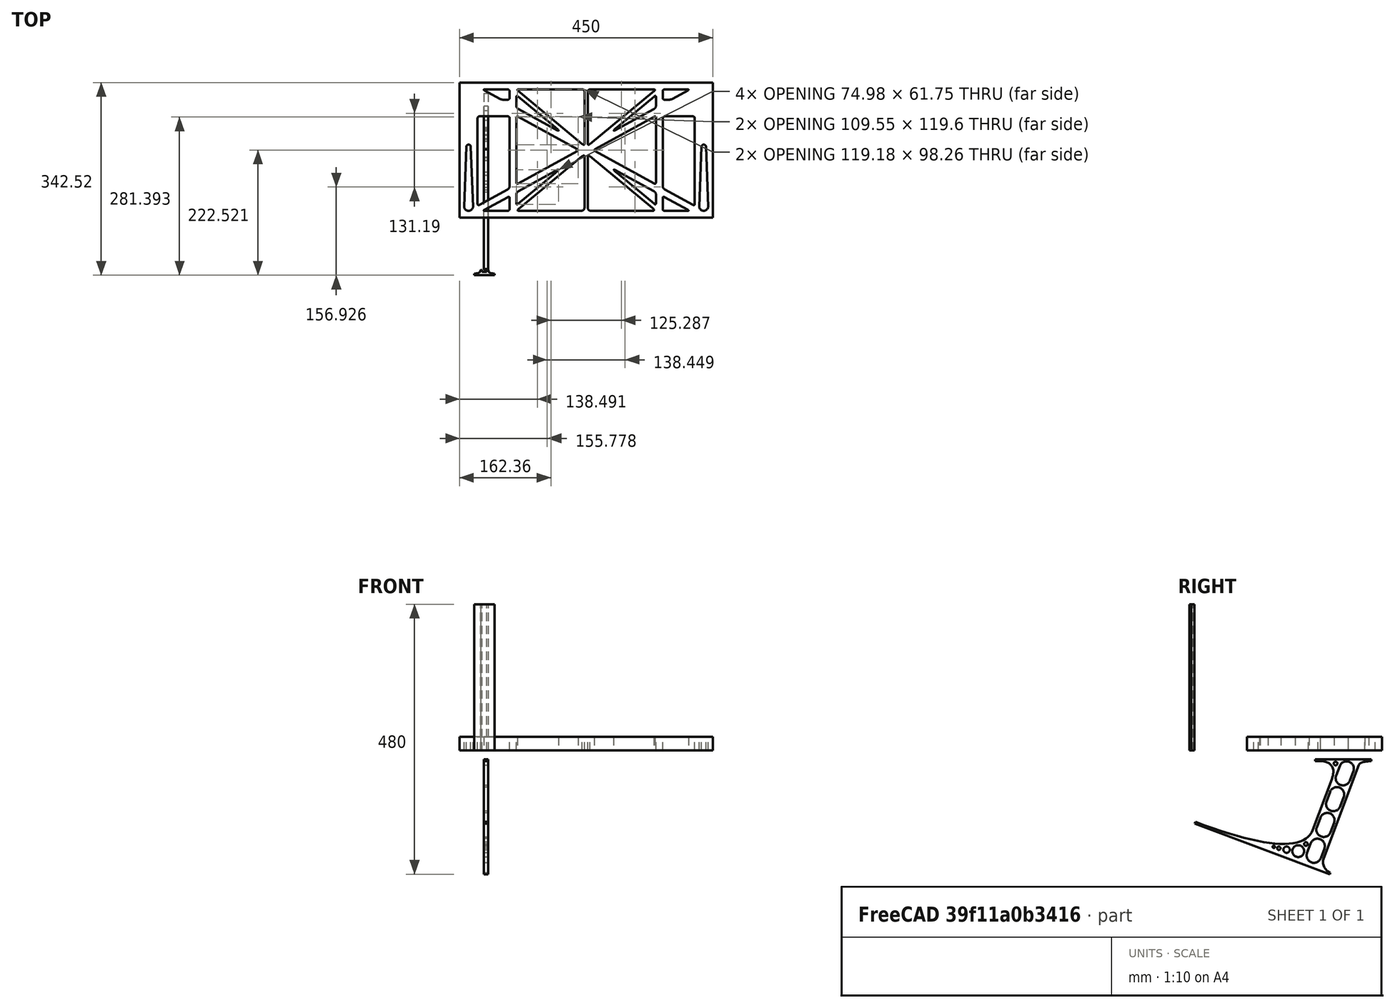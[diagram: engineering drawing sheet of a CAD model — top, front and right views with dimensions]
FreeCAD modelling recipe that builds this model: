
FCSTD DOCUMENT  (FreeCAD 0.19R0.19.2)
Label: laptopStand166FCStd
License: All rights reserved
LicenseURL: http://en.wikipedia.org/wiki/All_rights_reserved
objects: Sketcher::SketchObject×4, Part::Extrusion×3
note: 7 computed .brp shape members not serialized (recipe doc carries the construction recipe); baked Part::Feature solids carry a one-line shape summary decoded from their .brp

FEATURE [Sketcher::SketchObject] Sketch
  FullyConstrained = false
  sketch-geometry (349):
    g0: LineSegment StartX=-10.9272 StartY=-82.7794 StartZ=0 EndX=46.0728 EndY=-51.4823 EndZ=0
    g1: LineSegment StartX=-10.9272 StartY=76.4095 StartZ=0 EndX=-10.9272 EndY=-82.7794 EndZ=0
    g2: LineSegment StartX=46.0728 StartY=76.4095 StartZ=0 EndX=46.0728 EndY=-51.4823 EndZ=0
    g3: LineSegment StartX=-42.9272 StartY=136.221 StartZ=0 EndX=-42.9272 EndY=-103.779 EndZ=0
    g4: LineSegment StartX=407.073 StartY=136.221 StartZ=0 EndX=407.073 EndY=-103.779 EndZ=0
    g5: ArcOfCircle CenterX=-26.9272 CenterY=-83.7794 CenterZ=0 NormalX=0 NormalY=0 NormalZ=1 AngleXU=0 Radius=8 StartAngle=3.14159 EndAngle=6.28319
    g6: ArcOfCircle CenterX=391.073 CenterY=22.1087 CenterZ=0 NormalX=0 NormalY=0 NormalZ=1 AngleXU=0 Radius=8 StartAngle=-4.4e-15 EndAngle=3.14159
    g7: LineSegment StartX=399.073 StartY=22.1087 StartZ=0 EndX=399.073 EndY=-83.7794 EndZ=0
    g8: LineSegment StartX=383.073 StartY=22.1087 StartZ=0 EndX=383.073 EndY=-83.7794 EndZ=0
    g9: ArcOfCircle CenterX=391.073 CenterY=-83.7794 CenterZ=0 NormalX=0 NormalY=0 NormalZ=1 AngleXU=0 Radius=8 StartAngle=3.14159 EndAngle=6.28319
    g10: Circle CenterX=175.022 CenterY=27.0628 CenterZ=0 NormalX=0 NormalY=0 NormalZ=1 AngleXU=0 Radius=1
    g11: Circle CenterX=179.022 CenterY=24.8665 CenterZ=0 NormalX=0 NormalY=0 NormalZ=1 AngleXU=0 Radius=1
    g12: Circle CenterX=179.022 CenterY=27.0628 CenterZ=0 NormalX=0 NormalY=0 NormalZ=1 AngleXU=0 Radius=1
    g13: BSplineCurve PolesCount=3 KnotsCount=2 Degree=2 IsPeriodic=0
    g14: GeomPoint X=175.022 Y=27.0628 Z=0
    g15: GeomPoint X=179.022 Y=27.0628 Z=0
    g16: Circle CenterX=189.124 CenterY=27.0628 CenterZ=0 NormalX=0 NormalY=0 NormalZ=1 AngleXU=0 Radius=1
    g17: Circle CenterX=185.124 CenterY=24.8665 CenterZ=0 NormalX=0 NormalY=0 NormalZ=1 AngleXU=0 Radius=1
    g18: Circle CenterX=185.124 CenterY=27.0628 CenterZ=0 NormalX=0 NormalY=0 NormalZ=1 AngleXU=0 Radius=1
    g19: BSplineCurve PolesCount=3 KnotsCount=2 Degree=2 IsPeriodic=0
    g20: GeomPoint X=189.124 Y=27.0628 Z=0
    g21: GeomPoint X=185.124 Y=27.0628 Z=0
    g22: Circle CenterX=175.022 CenterY=5.37834 CenterZ=0 NormalX=0 NormalY=0 NormalZ=1 AngleXU=0 Radius=1
    g23: Circle CenterX=179.022 CenterY=7.57463 CenterZ=0 NormalX=0 NormalY=0 NormalZ=1 AngleXU=0 Radius=1
    g24: Circle CenterX=179.022 CenterY=5.34704 CenterZ=0 NormalX=0 NormalY=0 NormalZ=1 AngleXU=0 Radius=1
    g25: BSplineCurve PolesCount=3 KnotsCount=2 Degree=2 IsPeriodic=0
    g26: GeomPoint X=175.022 Y=5.37834 Z=0
    g27: GeomPoint X=179.022 Y=5.34704 Z=0
    g28: Circle CenterX=189.124 CenterY=5.37834 CenterZ=0 NormalX=0 NormalY=0 NormalZ=1 AngleXU=0 Radius=1
    g29: Circle CenterX=185.124 CenterY=7.57463 CenterZ=0 NormalX=0 NormalY=0 NormalZ=1 AngleXU=0 Radius=1
    g30: Circle CenterX=185.124 CenterY=5.34704 CenterZ=0 NormalX=0 NormalY=0 NormalZ=1 AngleXU=0 Radius=1
    g31: BSplineCurve PolesCount=3 KnotsCount=2 Degree=2 IsPeriodic=0
    g32: GeomPoint X=189.124 Y=5.37834 Z=0
    g33: GeomPoint X=185.124 Y=5.34704 Z=0
    g34: Circle CenterX=165.871 CenterY=18.1458 CenterZ=0 NormalX=0 NormalY=0 NormalZ=1 AngleXU=0 Radius=1
    g35: Circle CenterX=169.377 CenterY=16.2206 CenterZ=0 NormalX=0 NormalY=0 NormalZ=1 AngleXU=0 Radius=1
    g36: Circle CenterX=165.871 CenterY=14.2954 CenterZ=0 NormalX=0 NormalY=0 NormalZ=1 AngleXU=0 Radius=1
    g37: BSplineCurve PolesCount=3 KnotsCount=2 Degree=2 IsPeriodic=0
    g38: GeomPoint X=165.871 Y=18.1458 Z=0
    g39: GeomPoint X=165.871 Y=14.2954 Z=0
    g40: Circle CenterX=198.275 CenterY=18.1458 CenterZ=0 NormalX=0 NormalY=0 NormalZ=1 AngleXU=0 Radius=1
    g41: Circle CenterX=194.768 CenterY=16.2206 CenterZ=0 NormalX=0 NormalY=0 NormalZ=1 AngleXU=0 Radius=1
    g42: Circle CenterX=198.275 CenterY=14.2954 CenterZ=0 NormalX=0 NormalY=0 NormalZ=1 AngleXU=0 Radius=1
    g43: BSplineCurve PolesCount=3 KnotsCount=2 Degree=2 IsPeriodic=0
    g44: GeomPoint X=198.275 Y=18.1458 Z=0
    g45: GeomPoint X=198.275 Y=14.2954 Z=0
    g46: LineSegment StartX=407.073 StartY=-103.779 StartZ=0 EndX=-42.9272 EndY=-103.779 EndZ=0
    g47: LineSegment StartX=407.073 StartY=136.221 StartZ=0 EndX=-42.9272 EndY=136.221 EndZ=0
    g48: LineSegment StartX=46.0728 StartY=76.4095 StartZ=0 EndX=-10.9272 EndY=76.4095 EndZ=0
    g49: Circle CenterX=125.607 CenterY=54.1951 CenterZ=0 NormalX=0 NormalY=0 NormalZ=1 AngleXU=0 Radius=1
    g50: Circle CenterX=139.632 CenterY=46.4944 CenterZ=0 NormalX=0 NormalY=0 NormalZ=1 AngleXU=0 Radius=1
    g51: Circle CenterX=127.326 CenterY=56.7187 CenterZ=0 NormalX=0 NormalY=0 NormalZ=1 AngleXU=0 Radius=1
    g52: BSplineCurve PolesCount=3 KnotsCount=2 Degree=2 IsPeriodic=0
    g53: GeomPoint X=125.607 Y=54.1951 Z=0
    g54: GeomPoint X=127.326 Y=56.7187 Z=0
    g55: Circle CenterX=236.821 CenterY=56.7187 CenterZ=0 NormalX=0 NormalY=0 NormalZ=1 AngleXU=0 Radius=1
    g56: Circle CenterX=224.513 CenterY=46.4944 CenterZ=0 NormalX=0 NormalY=0 NormalZ=1 AngleXU=0 Radius=1
    g57: Circle CenterX=238.538 CenterY=54.1951 CenterZ=0 NormalX=0 NormalY=0 NormalZ=1 AngleXU=0 Radius=1
    g58: BSplineCurve PolesCount=3 KnotsCount=2 Degree=2 IsPeriodic=0
    g59: GeomPoint X=236.821 Y=56.7187 Z=0
    g60: GeomPoint X=238.538 Y=54.1951 Z=0
    g61: Circle CenterX=238.538 CenterY=-21.7539 CenterZ=0 NormalX=0 NormalY=0 NormalZ=1 AngleXU=0 Radius=1
    g62: Circle CenterX=224.513 CenterY=-14.0532 CenterZ=0 NormalX=0 NormalY=0 NormalZ=1 AngleXU=0 Radius=1
    g63: Circle CenterX=236.821 CenterY=-24.2775 CenterZ=0 NormalX=0 NormalY=0 NormalZ=1 AngleXU=0 Radius=1
    g64: BSplineCurve PolesCount=3 KnotsCount=2 Degree=2 IsPeriodic=0
    g65: GeomPoint X=238.538 Y=-21.7539 Z=0
    g66: GeomPoint X=236.821 Y=-24.2775 Z=0
    g67: Circle CenterX=125.607 CenterY=-21.7539 CenterZ=0 NormalX=0 NormalY=0 NormalZ=1 AngleXU=0 Radius=1
    g68: Circle CenterX=139.632 CenterY=-14.0532 CenterZ=0 NormalX=0 NormalY=0 NormalZ=1 AngleXU=0 Radius=1
    g69: Circle CenterX=127.325 CenterY=-24.2775 CenterZ=0 NormalX=0 NormalY=0 NormalZ=1 AngleXU=0 Radius=1
    g70: BSplineCurve PolesCount=3 KnotsCount=2 Degree=2 IsPeriodic=0
    g71: GeomPoint X=125.607 Y=-21.7539 Z=0
    g72: GeomPoint X=127.325 Y=-24.2775 Z=0
    g73: Circle CenterX=302.996 CenterY=111.695 CenterZ=0 NormalX=0 NormalY=0 NormalZ=1 AngleXU=0 Radius=1
    g74: Circle CenterX=306.073 CenterY=114.251 CenterZ=0 NormalX=0 NormalY=0 NormalZ=1 AngleXU=0 Radius=1
    g75: Circle CenterX=306.073 CenterY=110.251 CenterZ=0 NormalX=0 NormalY=0 NormalZ=1 AngleXU=0 Radius=1
    g76: BSplineCurve PolesCount=3 KnotsCount=2 Degree=2 IsPeriodic=0
    g77: GeomPoint X=302.996 Y=111.695 Z=0
    g78: GeomPoint X=306.073 Y=110.251 Z=0
    g79: Circle CenterX=306.073 CenterY=95.2763 CenterZ=0 NormalX=0 NormalY=0 NormalZ=1 AngleXU=0 Radius=1
    g80: Circle CenterX=306.073 CenterY=91.2763 CenterZ=0 NormalX=0 NormalY=0 NormalZ=1 AngleXU=0 Radius=1
    g81: Circle CenterX=302.567 CenterY=89.3511 CenterZ=0 NormalX=0 NormalY=0 NormalZ=1 AngleXU=0 Radius=1
    g82: BSplineCurve PolesCount=3 KnotsCount=2 Degree=2 IsPeriodic=0
    g83: GeomPoint X=306.073 Y=95.2763 Z=0
    g84: GeomPoint X=302.567 Y=89.3511 Z=0
    g85: LineSegment StartX=306.073 StartY=110.251 StartZ=0 EndX=306.073 EndY=95.2763 EndZ=0
    g86: LineSegment StartX=302.996 StartY=111.695 StartZ=0 EndX=236.821 EndY=56.7187 EndZ=0
    g87: LineSegment StartX=238.538 StartY=54.1951 StartZ=0 EndX=302.567 EndY=89.3511 EndZ=0
    g88: Circle CenterX=61.1496 CenterY=111.695 CenterZ=0 NormalX=0 NormalY=0 NormalZ=1 AngleXU=0 Radius=1
    g89: Circle CenterX=58.0728 CenterY=114.251 CenterZ=0 NormalX=0 NormalY=0 NormalZ=1 AngleXU=0 Radius=1
    g90: Circle CenterX=58.0728 CenterY=110.251 CenterZ=0 NormalX=0 NormalY=0 NormalZ=1 AngleXU=0 Radius=1
    g91: BSplineCurve PolesCount=3 KnotsCount=2 Degree=2 IsPeriodic=0
    g92: GeomPoint X=61.1496 Y=111.695 Z=0
    g93: GeomPoint X=58.0728 Y=110.251 Z=0
    g94: Circle CenterX=61.5791 CenterY=89.3511 CenterZ=0 NormalX=0 NormalY=0 NormalZ=1 AngleXU=0 Radius=1
    g95: Circle CenterX=58.0728 CenterY=91.2763 CenterZ=0 NormalX=0 NormalY=0 NormalZ=1 AngleXU=0 Radius=1
    g96: Circle CenterX=58.0728 CenterY=95.2763 CenterZ=0 NormalX=0 NormalY=0 NormalZ=1 AngleXU=0 Radius=1
    g97: BSplineCurve PolesCount=3 KnotsCount=2 Degree=2 IsPeriodic=0
    g98: GeomPoint X=61.5791 Y=89.3511 Z=0
    g99: GeomPoint X=58.0728 Y=95.2763 Z=0
    g100: LineSegment StartX=58.0728 StartY=110.251 StartZ=0 EndX=58.0728 EndY=95.2763 EndZ=0
    g101: LineSegment StartX=61.1496 StartY=111.695 StartZ=0 EndX=127.326 EndY=56.7187 EndZ=0
    g102: LineSegment StartX=125.607 StartY=54.1951 StartZ=0 EndX=61.5791 EndY=89.3511 EndZ=0
    g103: Circle CenterX=61.5791 CenterY=-56.9099 CenterZ=0 NormalX=0 NormalY=0 NormalZ=1 AngleXU=0 Radius=1
    g104: Circle CenterX=58.0728 CenterY=-58.8351 CenterZ=0 NormalX=0 NormalY=0 NormalZ=1 AngleXU=0 Radius=1
    g105: Circle CenterX=58.0728 CenterY=-62.8351 CenterZ=0 NormalX=0 NormalY=0 NormalZ=1 AngleXU=0 Radius=1
    g106: BSplineCurve PolesCount=3 KnotsCount=2 Degree=2 IsPeriodic=0
    g107: GeomPoint X=61.5791 Y=-56.9099 Z=0
    g108: GeomPoint X=58.0728 Y=-62.8351 Z=0
    g109: Circle CenterX=58.0728 CenterY=-77.8102 CenterZ=0 NormalX=0 NormalY=0 NormalZ=1 AngleXU=0 Radius=1
    g110: Circle CenterX=58.0728 CenterY=-81.8102 CenterZ=0 NormalX=0 NormalY=0 NormalZ=1 AngleXU=0 Radius=1
    g111: Circle CenterX=61.1496 CenterY=-79.2541 CenterZ=0 NormalX=0 NormalY=0 NormalZ=1 AngleXU=0 Radius=1
    g112: BSplineCurve PolesCount=3 KnotsCount=2 Degree=2 IsPeriodic=0
    g113: GeomPoint X=58.0728 Y=-77.8102 Z=0
    g114: GeomPoint X=61.1496 Y=-79.2541 Z=0
    g115: LineSegment StartX=58.0728 StartY=-62.8351 StartZ=0 EndX=58.0728 EndY=-77.8102 EndZ=0
    g116: LineSegment StartX=61.1496 StartY=-79.2541 StartZ=0 EndX=127.325 EndY=-24.2775 EndZ=0
    g117: LineSegment StartX=125.607 StartY=-21.7539 StartZ=0 EndX=61.5791 EndY=-56.9099 EndZ=0
    g118: Circle CenterX=302.567 CenterY=-56.9099 CenterZ=0 NormalX=0 NormalY=0 NormalZ=1 AngleXU=0 Radius=1
    g119: Circle CenterX=306.073 CenterY=-58.8351 CenterZ=0 NormalX=0 NormalY=0 NormalZ=1 AngleXU=0 Radius=1
    g120: Circle CenterX=306.073 CenterY=-62.8351 CenterZ=0 NormalX=0 NormalY=0 NormalZ=1 AngleXU=0 Radius=1
    g121: BSplineCurve PolesCount=3 KnotsCount=2 Degree=2 IsPeriodic=0
    g122: GeomPoint X=302.567 Y=-56.9099 Z=0
    g123: GeomPoint X=306.073 Y=-62.8351 Z=0
    g124: Circle CenterX=302.996 CenterY=-79.2541 CenterZ=0 NormalX=0 NormalY=0 NormalZ=1 AngleXU=0 Radius=1
    g125: Circle CenterX=306.073 CenterY=-81.8102 CenterZ=0 NormalX=0 NormalY=0 NormalZ=1 AngleXU=0 Radius=1
    g126: Circle CenterX=306.073 CenterY=-77.8102 CenterZ=0 NormalX=0 NormalY=0 NormalZ=1 AngleXU=0 Radius=1
    g127: BSplineCurve PolesCount=3 KnotsCount=2 Degree=2 IsPeriodic=0
    g128: GeomPoint X=302.996 Y=-79.2541 Z=0
    g129: GeomPoint X=306.073 Y=-77.8102 Z=0
    g130: LineSegment StartX=306.073 StartY=-62.8351 StartZ=0 EndX=306.073 EndY=-77.8102 EndZ=0
    g131: LineSegment StartX=302.996 StartY=-79.2541 StartZ=0 EndX=236.821 EndY=-24.2775 EndZ=0
    g132: LineSegment StartX=238.538 StartY=-21.7539 StartZ=0 EndX=302.567 EndY=-56.9099 EndZ=0
    g133: Circle CenterX=61.6457 CenterY=-88.8112 CenterZ=0 NormalX=0 NormalY=0 NormalZ=1 AngleXU=0 Radius=1
    g134: Circle CenterX=58.0728 CenterY=-91.7794 CenterZ=0 NormalX=0 NormalY=0 NormalZ=1 AngleXU=0 Radius=1
    g135: Circle CenterX=63.9135 CenterY=-91.7794 CenterZ=0 NormalX=0 NormalY=0 NormalZ=1 AngleXU=0 Radius=1
    g136: BSplineCurve PolesCount=3 KnotsCount=2 Degree=2 IsPeriodic=0
    g137: GeomPoint X=61.6457 Y=-88.8112 Z=0
    g138: GeomPoint X=63.9135 Y=-91.7794 Z=0
    g139: Circle CenterX=179.022 CenterY=-85.8163 CenterZ=0 NormalX=0 NormalY=0 NormalZ=1 AngleXU=0 Radius=1
    g140: Circle CenterX=179.022 CenterY=-91.7794 CenterZ=0 NormalX=0 NormalY=0 NormalZ=1 AngleXU=0 Radius=1
    g141: Circle CenterX=171.895 CenterY=-91.7794 CenterZ=0 NormalX=0 NormalY=0 NormalZ=1 AngleXU=0 Radius=1
    g142: BSplineCurve PolesCount=3 KnotsCount=2 Degree=2 IsPeriodic=0
    g143: GeomPoint X=179.022 Y=-85.8163 Z=0
    g144: GeomPoint X=171.895 Y=-91.7794 Z=0
    g145: Circle CenterX=185.124 CenterY=-86.2028 CenterZ=0 NormalX=0 NormalY=0 NormalZ=1 AngleXU=0 Radius=1
    g146: Circle CenterX=185.124 CenterY=-91.7794 CenterZ=0 NormalX=0 NormalY=0 NormalZ=1 AngleXU=0 Radius=1
    g147: Circle CenterX=191.747 CenterY=-91.7794 CenterZ=0 NormalX=0 NormalY=0 NormalZ=1 AngleXU=0 Radius=1
    g148: BSplineCurve PolesCount=3 KnotsCount=2 Degree=2 IsPeriodic=0
    g149: GeomPoint X=185.124 Y=-86.2028 Z=0
    g150: GeomPoint X=191.747 Y=-91.7794 Z=0
    g151: Circle CenterX=299.888 CenterY=-86.6413 CenterZ=0 NormalX=0 NormalY=0 NormalZ=1 AngleXU=0 Radius=1
    g152: Circle CenterX=306.073 CenterY=-91.7794 CenterZ=0 NormalX=0 NormalY=0 NormalZ=1 AngleXU=0 Radius=1
    g153: Circle CenterX=298.776 CenterY=-91.7794 CenterZ=0 NormalX=0 NormalY=0 NormalZ=1 AngleXU=0 Radius=1
    g154: BSplineCurve PolesCount=3 KnotsCount=2 Degree=2 IsPeriodic=0
    g155: GeomPoint X=299.888 Y=-86.6413 Z=0
    g156: GeomPoint X=298.776 Y=-91.7794 Z=0
    g157: LineSegment StartX=189.124 StartY=5.37834 StartZ=0 EndX=299.888 EndY=-86.6413 EndZ=0
    g158: LineSegment StartX=298.776 StartY=-91.7794 StartZ=0 EndX=191.747 EndY=-91.7794 EndZ=0
    g159: LineSegment StartX=185.124 StartY=-86.2028 StartZ=0 EndX=185.124 EndY=5.34704 EndZ=0
    g160: LineSegment StartX=179.022 StartY=5.34704 StartZ=0 EndX=179.022 EndY=-85.8163 EndZ=0
    g161: LineSegment StartX=171.895 StartY=-91.7794 StartZ=0 EndX=63.9135 EndY=-91.7794 EndZ=0
    g162: LineSegment StartX=61.6457 StartY=-88.8112 StartZ=0 EndX=175.022 EndY=5.37834 EndZ=0
    g163: Circle CenterX=302.073 CenterY=124.221 CenterZ=0 NormalX=0 NormalY=0 NormalZ=1 AngleXU=0 Radius=1
    g164: Circle CenterX=306.073 CenterY=124.221 CenterZ=0 NormalX=0 NormalY=0 NormalZ=1 AngleXU=0 Radius=1
    g165: Circle CenterX=302.996 CenterY=121.665 CenterZ=0 NormalX=0 NormalY=0 NormalZ=1 AngleXU=0 Radius=1
    g166: BSplineCurve PolesCount=3 KnotsCount=2 Degree=2 IsPeriodic=0
    g167: GeomPoint X=302.073 Y=124.221 Z=0
    g168: GeomPoint X=302.996 Y=121.665 Z=0
    g169: Circle CenterX=189.124 CenterY=124.221 CenterZ=0 NormalX=0 NormalY=0 NormalZ=1 AngleXU=0 Radius=1
    g170: Circle CenterX=185.124 CenterY=124.221 CenterZ=0 NormalX=0 NormalY=0 NormalZ=1 AngleXU=0 Radius=1
    g171: Circle CenterX=185.124 CenterY=120.221 CenterZ=0 NormalX=0 NormalY=0 NormalZ=1 AngleXU=0 Radius=1
    g172: BSplineCurve PolesCount=3 KnotsCount=2 Degree=2 IsPeriodic=0
    g173: GeomPoint X=189.124 Y=124.221 Z=0
    g174: GeomPoint X=185.124 Y=120.221 Z=0
    g175: Circle CenterX=175.022 CenterY=124.221 CenterZ=0 NormalX=0 NormalY=0 NormalZ=1 AngleXU=0 Radius=1
    g176: Circle CenterX=179.022 CenterY=124.221 CenterZ=0 NormalX=0 NormalY=0 NormalZ=1 AngleXU=0 Radius=1
    g177: Circle CenterX=179.022 CenterY=120.221 CenterZ=0 NormalX=0 NormalY=0 NormalZ=1 AngleXU=0 Radius=1
    g178: BSplineCurve PolesCount=3 KnotsCount=2 Degree=2 IsPeriodic=0
    g179: GeomPoint X=175.022 Y=124.221 Z=0
    g180: GeomPoint X=179.022 Y=120.221 Z=0
    g181: Circle CenterX=62.0728 CenterY=124.221 CenterZ=0 NormalX=0 NormalY=0 NormalZ=1 AngleXU=0 Radius=1
    g182: Circle CenterX=58.0728 CenterY=124.221 CenterZ=0 NormalX=0 NormalY=0 NormalZ=1 AngleXU=0 Radius=1
    g183: Circle CenterX=61.1496 CenterY=121.665 CenterZ=0 NormalX=0 NormalY=0 NormalZ=1 AngleXU=0 Radius=1
    g184: BSplineCurve PolesCount=3 KnotsCount=2 Degree=2 IsPeriodic=0
    g185: GeomPoint X=62.0728 Y=124.221 Z=0
    g186: GeomPoint X=61.1496 Y=121.665 Z=0
    g187: LineSegment StartX=62.0728 StartY=124.221 StartZ=0 EndX=175.022 EndY=124.221 EndZ=0
    g188: LineSegment StartX=179.022 StartY=120.221 StartZ=0 EndX=179.022 EndY=27.0628 EndZ=0
    g189: LineSegment StartX=185.124 StartY=27.0628 StartZ=0 EndX=185.124 EndY=120.221 EndZ=0
    g190: LineSegment StartX=189.124 StartY=124.221 StartZ=0 EndX=302.073 EndY=124.221 EndZ=0
    g191: LineSegment StartX=302.996 StartY=121.665 StartZ=0 EndX=189.124 EndY=27.0628 EndZ=0
    g192: LineSegment StartX=175.022 StartY=27.0628 StartZ=0 EndX=61.1496 EndY=121.665 EndZ=0
    g193: Circle CenterX=61.5791 CenterY=75.4095 CenterZ=0 NormalX=0 NormalY=0 NormalZ=1 AngleXU=0 Radius=1
    g194: Circle CenterX=58.0728 CenterY=77.3346 CenterZ=0 NormalX=0 NormalY=0 NormalZ=1 AngleXU=0 Radius=1
    g195: Circle CenterX=58.0728 CenterY=73.3346 CenterZ=0 NormalX=0 NormalY=0 NormalZ=1 AngleXU=0 Radius=1
    g196: BSplineCurve PolesCount=3 KnotsCount=2 Degree=2 IsPeriodic=0
    g197: GeomPoint X=61.5791 Y=75.4095 Z=0
    g198: GeomPoint X=58.0728 Y=73.3346 Z=0
    g199: Circle CenterX=58.0728 CenterY=-40.8935 CenterZ=0 NormalX=0 NormalY=0 NormalZ=1 AngleXU=0 Radius=1
    g200: Circle CenterX=58.0728 CenterY=-44.8935 CenterZ=0 NormalX=0 NormalY=0 NormalZ=1 AngleXU=0 Radius=1
    g201: Circle CenterX=61.5791 CenterY=-42.9683 CenterZ=0 NormalX=0 NormalY=0 NormalZ=1 AngleXU=0 Radius=1
    g202: BSplineCurve PolesCount=3 KnotsCount=2 Degree=2 IsPeriodic=0
    g203: GeomPoint X=58.0728 Y=-40.8935 Z=0
    g204: GeomPoint X=61.5791 Y=-42.9683 Z=0
    g205: LineSegment StartX=61.5791 StartY=-42.9683 StartZ=0 EndX=165.871 EndY=14.2954 EndZ=0
    g206: LineSegment StartX=165.871 StartY=18.1458 StartZ=0 EndX=61.5791 EndY=75.4095 EndZ=0
    g207: LineSegment StartX=58.0728 StartY=73.3346 StartZ=0 EndX=58.0728 EndY=-40.8935 EndZ=0
    g208: Circle CenterX=302.567 CenterY=-42.9683 CenterZ=0 NormalX=0 NormalY=0 NormalZ=1 AngleXU=0 Radius=1
    g209: Circle CenterX=306.073 CenterY=-44.8935 CenterZ=0 NormalX=0 NormalY=0 NormalZ=1 AngleXU=0 Radius=1
    g210: Circle CenterX=306.073 CenterY=-40.8935 CenterZ=0 NormalX=0 NormalY=0 NormalZ=1 AngleXU=0 Radius=1
    g211: BSplineCurve PolesCount=3 KnotsCount=2 Degree=2 IsPeriodic=0
    g212: GeomPoint X=302.567 Y=-42.9683 Z=0
    g213: GeomPoint X=306.073 Y=-40.8935 Z=0
    g214: Circle CenterX=306.073 CenterY=73.3346 CenterZ=0 NormalX=0 NormalY=0 NormalZ=1 AngleXU=0 Radius=1
    g215: Circle CenterX=306.073 CenterY=77.3346 CenterZ=0 NormalX=0 NormalY=0 NormalZ=1 AngleXU=0 Radius=1
    g216: Circle CenterX=302.567 CenterY=75.4095 CenterZ=0 NormalX=0 NormalY=0 NormalZ=1 AngleXU=0 Radius=1
    g217: BSplineCurve PolesCount=3 KnotsCount=2 Degree=2 IsPeriodic=0
    g218: GeomPoint X=306.073 Y=73.3346 Z=0
    g219: GeomPoint X=302.567 Y=75.4095 Z=0
    g220: LineSegment StartX=302.567 StartY=-42.9683 StartZ=0 EndX=198.275 EndY=14.2954 EndZ=0
    g221: LineSegment StartX=198.275 StartY=18.1458 StartZ=0 EndX=302.567 EndY=75.4095 EndZ=0
    g222: LineSegment StartX=306.073 StartY=73.3346 StartZ=0 EndX=306.073 EndY=-40.8935 EndZ=0
    g223: LineSegment StartX=322.073 StartY=105.865 StartZ=0 EndX=328.643 EndY=105.865 EndZ=0
    g224: LineSegment StartX=318.073 StartY=120.221 StartZ=0 EndX=318.073 EndY=109.865 EndZ=0
    g225: LineSegment StartX=336.157 StartY=107.779 StartZ=0 EndX=362.567 EndY=122.294 EndZ=0
    g226: Circle CenterX=362.073 CenterY=124.221 CenterZ=0 NormalX=0 NormalY=0 NormalZ=1 AngleXU=0 Radius=1
    g227: Circle CenterX=366.073 CenterY=124.221 CenterZ=0 NormalX=0 NormalY=0 NormalZ=1 AngleXU=0 Radius=1
    g228: Circle CenterX=362.567 CenterY=122.294 CenterZ=0 NormalX=0 NormalY=0 NormalZ=1 AngleXU=0 Radius=1
    g229: BSplineCurve PolesCount=3 KnotsCount=2 Degree=2 IsPeriodic=0
    g230: GeomPoint X=362.073 Y=124.221 Z=0
    g231: GeomPoint X=362.567 Y=122.294 Z=0
    g232: Circle CenterX=322.073 CenterY=124.221 CenterZ=0 NormalX=0 NormalY=0 NormalZ=1 AngleXU=0 Radius=1
    g233: Circle CenterX=318.073 CenterY=124.221 CenterZ=0 NormalX=0 NormalY=0 NormalZ=1 AngleXU=0 Radius=1
    g234: Circle CenterX=318.073 CenterY=120.221 CenterZ=0 NormalX=0 NormalY=0 NormalZ=1 AngleXU=0 Radius=1
    g235: BSplineCurve PolesCount=3 KnotsCount=2 Degree=2 IsPeriodic=0
    g236: GeomPoint X=322.073 Y=124.221 Z=0
    g237: GeomPoint X=318.073 Y=120.221 Z=0
    g238: Circle CenterX=322.073 CenterY=105.865 CenterZ=0 NormalX=0 NormalY=0 NormalZ=1 AngleXU=0 Radius=1
    g239: Circle CenterX=318.073 CenterY=105.865 CenterZ=0 NormalX=0 NormalY=0 NormalZ=1 AngleXU=0 Radius=1
    g240: Circle CenterX=318.073 CenterY=109.865 CenterZ=0 NormalX=0 NormalY=0 NormalZ=1 AngleXU=0 Radius=1
    g241: BSplineCurve PolesCount=3 KnotsCount=2 Degree=2 IsPeriodic=0
    g242: GeomPoint X=322.073 Y=105.865 Z=0
    g243: GeomPoint X=318.073 Y=109.865 Z=0
    g244: Circle CenterX=336.157 CenterY=107.779 CenterZ=0 NormalX=0 NormalY=0 NormalZ=1 AngleXU=0 Radius=1
    g245: Circle CenterX=332.651 CenterY=105.853 CenterZ=0 NormalX=0 NormalY=0 NormalZ=1 AngleXU=0 Radius=1
    g246: Circle CenterX=328.643 CenterY=105.865 CenterZ=0 NormalX=0 NormalY=0 NormalZ=1 AngleXU=0 Radius=1
    g247: BSplineCurve PolesCount=3 KnotsCount=2 Degree=2 IsPeriodic=0
    g248: GeomPoint X=336.157 Y=107.779 Z=0
    g249: GeomPoint X=328.643 Y=105.865 Z=0
    g250: LineSegment StartX=322.073 StartY=124.221 StartZ=0 EndX=362.073 EndY=124.221 EndZ=0
    g251: Circle CenterX=371.567 CenterY=-80.8644 CenterZ=0 NormalX=0 NormalY=0 NormalZ=1 AngleXU=0 Radius=1
    g252: Circle CenterX=375.073 CenterY=-82.7896 CenterZ=0 NormalX=0 NormalY=0 NormalZ=1 AngleXU=0 Radius=1
    g253: Circle CenterX=375.073 CenterY=-78.7896 CenterZ=0 NormalX=0 NormalY=0 NormalZ=1 AngleXU=0 Radius=1
    g254: BSplineCurve PolesCount=3 KnotsCount=2 Degree=2 IsPeriodic=0
    g255: GeomPoint X=371.567 Y=-80.8644 Z=0
    g256: GeomPoint X=375.073 Y=-78.7896 Z=0
    g257: Circle CenterX=321.579 CenterY=-53.4075 CenterZ=0 NormalX=0 NormalY=0 NormalZ=1 AngleXU=0 Radius=1
    g258: Circle CenterX=318.073 CenterY=-51.4823 CenterZ=0 NormalX=0 NormalY=0 NormalZ=1 AngleXU=0 Radius=1
    g259: Circle CenterX=318.073 CenterY=-47.4805 CenterZ=0 NormalX=0 NormalY=0 NormalZ=1 AngleXU=0 Radius=1
    g260: BSplineCurve PolesCount=3 KnotsCount=2 Degree=2 IsPeriodic=0
    g261: GeomPoint X=321.579 Y=-53.4075 Z=0
    g262: GeomPoint X=318.073 Y=-47.4805 Z=0
    g263: LineSegment StartX=371.567 StartY=-80.8644 StartZ=0 EndX=321.579 EndY=-53.4075 EndZ=0
    g264: Circle CenterX=321.579 CenterY=-67.3492 CenterZ=0 NormalX=0 NormalY=0 NormalZ=1 AngleXU=0 Radius=1
    g265: Circle CenterX=318.073 CenterY=-65.424 CenterZ=0 NormalX=0 NormalY=0 NormalZ=1 AngleXU=0 Radius=1
    g266: Circle CenterX=318.073 CenterY=-69.424 CenterZ=0 NormalX=0 NormalY=0 NormalZ=1 AngleXU=0 Radius=1
    g267: BSplineCurve PolesCount=3 KnotsCount=2 Degree=2 IsPeriodic=0
    g268: GeomPoint X=321.579 Y=-67.3492 Z=0
    g269: GeomPoint X=318.073 Y=-69.424 Z=0
    g270: Circle CenterX=362.567 CenterY=-89.8542 CenterZ=0 NormalX=0 NormalY=0 NormalZ=1 AngleXU=0 Radius=1
    g271: Circle CenterX=366.073 CenterY=-91.7794 CenterZ=0 NormalX=0 NormalY=0 NormalZ=1 AngleXU=0 Radius=1
    g272: Circle CenterX=362.073 CenterY=-91.7794 CenterZ=0 NormalX=0 NormalY=0 NormalZ=1 AngleXU=0 Radius=1
    g273: BSplineCurve PolesCount=3 KnotsCount=2 Degree=2 IsPeriodic=0
    g274: GeomPoint X=362.567 Y=-89.8542 Z=0
    g275: GeomPoint X=362.073 Y=-91.7794 Z=0
    g276: Circle CenterX=322.073 CenterY=-91.7794 CenterZ=0 NormalX=0 NormalY=0 NormalZ=1 AngleXU=0 Radius=1
    g277: Circle CenterX=318.073 CenterY=-91.7794 CenterZ=0 NormalX=0 NormalY=0 NormalZ=1 AngleXU=0 Radius=1
    g278: Circle CenterX=318.073 CenterY=-87.7794 CenterZ=0 NormalX=0 NormalY=0 NormalZ=1 AngleXU=0 Radius=1
    g279: BSplineCurve PolesCount=3 KnotsCount=2 Degree=2 IsPeriodic=0
    g280: GeomPoint X=322.073 Y=-91.7794 Z=0
    g281: GeomPoint X=318.073 Y=-87.7794 Z=0
    g282: LineSegment StartX=362.567 StartY=-89.8542 StartZ=0 EndX=321.579 EndY=-67.3492 EndZ=0
    g283: LineSegment StartX=318.073 StartY=-69.424 StartZ=0 EndX=318.073 EndY=-87.7794 EndZ=0
    g284: LineSegment StartX=322.073 StartY=-91.7794 StartZ=0 EndX=362.073 EndY=-91.7794 EndZ=0
    g285: Circle CenterX=2.07281 CenterY=124.221 CenterZ=0 NormalX=0 NormalY=0 NormalZ=1 AngleXU=0 Radius=1
    g286: Circle CenterX=1.57905 CenterY=122.295 CenterZ=0 NormalX=0 NormalY=0 NormalZ=1 AngleXU=0 Radius=1
    g287: BSplineCurve PolesCount=3 KnotsCount=2 Degree=2 IsPeriodic=0
    g288: GeomPoint X=2.07281 Y=124.221 Z=0
    g289: GeomPoint X=1.57905 Y=122.295 Z=0
    g290: Circle CenterX=42.0728 CenterY=124.221 CenterZ=0 NormalX=0 NormalY=0 NormalZ=1 AngleXU=0 Radius=1
    g291: Circle CenterX=46.0728 CenterY=124.221 CenterZ=0 NormalX=0 NormalY=0 NormalZ=1 AngleXU=0 Radius=1
    g292: Circle CenterX=46.0728 CenterY=120.221 CenterZ=0 NormalX=0 NormalY=0 NormalZ=1 AngleXU=0 Radius=1
    g293: BSplineCurve PolesCount=3 KnotsCount=2 Degree=2 IsPeriodic=0
    g294: GeomPoint X=42.0728 Y=124.221 Z=0
    g295: GeomPoint X=46.0728 Y=120.221 Z=0
    g296: Circle CenterX=46.0728 CenterY=109.865 CenterZ=0 NormalX=0 NormalY=0 NormalZ=1 AngleXU=0 Radius=1
    g297: Circle CenterX=46.0728 CenterY=105.865 CenterZ=0 NormalX=0 NormalY=0 NormalZ=1 AngleXU=0 Radius=1
    g298: Circle CenterX=42.0728 CenterY=105.865 CenterZ=0 NormalX=0 NormalY=0 NormalZ=1 AngleXU=0 Radius=1
    g299: BSplineCurve PolesCount=3 KnotsCount=2 Degree=2 IsPeriodic=0
    g300: GeomPoint X=46.0728 Y=109.865 Z=0
    g301: GeomPoint X=42.0728 Y=105.865 Z=0
    g302: Circle CenterX=35.5028 CenterY=105.865 CenterZ=0 NormalX=0 NormalY=0 NormalZ=1 AngleXU=0 Radius=1
    g303: Circle CenterX=31.5028 CenterY=105.865 CenterZ=0 NormalX=0 NormalY=0 NormalZ=1 AngleXU=0 Radius=1
    g304: Circle CenterX=27.9965 CenterY=107.79 CenterZ=0 NormalX=0 NormalY=0 NormalZ=1 AngleXU=0 Radius=1
    g305: BSplineCurve PolesCount=3 KnotsCount=2 Degree=2 IsPeriodic=0
    g306: GeomPoint X=35.5028 Y=105.865 Z=0
    g307: GeomPoint X=27.9965 Y=107.79 Z=0
    g308: LineSegment StartX=2.07281 StartY=124.221 StartZ=0 EndX=42.0728 EndY=124.221 EndZ=0
    g309: LineSegment StartX=46.0728 StartY=120.221 StartZ=0 EndX=46.0728 EndY=109.865 EndZ=0
    g310: LineSegment StartX=42.0728 StartY=105.865 StartZ=0 EndX=35.5028 EndY=105.865 EndZ=0
    g311: LineSegment StartX=27.9965 StartY=107.79 StartZ=0 EndX=1.57905 EndY=122.295 EndZ=0
    g312: Circle CenterX=42.5666 CenterY=-67.3492 CenterZ=0 NormalX=0 NormalY=0 NormalZ=1 AngleXU=0 Radius=1
    g313: Circle CenterX=46.0728 CenterY=-65.424 CenterZ=0 NormalX=0 NormalY=0 NormalZ=1 AngleXU=0 Radius=1
    g314: Circle CenterX=46.0728 CenterY=-69.424 CenterZ=0 NormalX=0 NormalY=0 NormalZ=1 AngleXU=0 Radius=1
    g315: BSplineCurve PolesCount=3 KnotsCount=2 Degree=2 IsPeriodic=0
    g316: GeomPoint X=42.5666 Y=-67.3492 Z=0
    g317: GeomPoint X=46.0728 Y=-69.424 Z=0
    g318: Circle CenterX=46.0728 CenterY=-87.7794 CenterZ=0 NormalX=0 NormalY=0 NormalZ=1 AngleXU=0 Radius=1
    g319: Circle CenterX=46.0728 CenterY=-91.7794 CenterZ=0 NormalX=0 NormalY=0 NormalZ=1 AngleXU=0 Radius=1
    g320: Circle CenterX=42.0728 CenterY=-91.7794 CenterZ=0 NormalX=0 NormalY=0 NormalZ=1 AngleXU=0 Radius=1
    g321: BSplineCurve PolesCount=3 KnotsCount=2 Degree=2 IsPeriodic=0
    g322: GeomPoint X=46.0728 Y=-87.7794 Z=0
    g323: GeomPoint X=42.0728 Y=-91.7794 Z=0
    g324: Circle CenterX=2.07281 CenterY=-91.7794 CenterZ=0 NormalX=0 NormalY=0 NormalZ=1 AngleXU=0 Radius=1
    g325: Circle CenterX=-1.92719 CenterY=-91.7794 CenterZ=0 NormalX=0 NormalY=0 NormalZ=1 AngleXU=0 Radius=1
    g326: Circle CenterX=1.57905 CenterY=-89.8542 CenterZ=0 NormalX=0 NormalY=0 NormalZ=1 AngleXU=0 Radius=1
    g327: BSplineCurve PolesCount=3 KnotsCount=2 Degree=2 IsPeriodic=0
    g328: GeomPoint X=2.07281 Y=-91.7794 Z=0
    g329: GeomPoint X=1.57905 Y=-89.8542 Z=0
    g330: LineSegment StartX=2.07281 StartY=-91.7794 StartZ=0 EndX=42.0728 EndY=-91.7794 EndZ=0
    g331: LineSegment StartX=46.0728 StartY=-87.7794 StartZ=0 EndX=46.0728 EndY=-69.424 EndZ=0
    g332: LineSegment StartX=42.5666 StartY=-67.3492 StartZ=0 EndX=1.57905 EndY=-89.8542 EndZ=0
    g333: Circle CenterX=322.073 CenterY=76.4095 CenterZ=0 NormalX=0 NormalY=0 NormalZ=1 AngleXU=0 Radius=4
    g334: BSplineCurve PolesCount=3 KnotsCount=2 Degree=2 IsPeriodic=0
    g335: GeomPoint X=318.073 Y=72.4095 Z=0
    g336: GeomPoint X=322.073 Y=76.4095 Z=0
    g337: Circle CenterX=375.073 CenterY=72.4095 CenterZ=0 NormalX=0 NormalY=0 NormalZ=1 AngleXU=0 Radius=1
    g338: Circle CenterX=375.073 CenterY=76.4095 CenterZ=0 NormalX=0 NormalY=0 NormalZ=1 AngleXU=0 Radius=1
    g339: Circle CenterX=371.073 CenterY=76.4095 CenterZ=0 NormalX=0 NormalY=0 NormalZ=1 AngleXU=0 Radius=1
    g340: BSplineCurve PolesCount=3 KnotsCount=2 Degree=2 IsPeriodic=0
    g341: GeomPoint X=375.073 Y=72.4095 Z=0
    g342: GeomPoint X=371.073 Y=76.4095 Z=0
    g343: LineSegment StartX=322.073 StartY=76.4095 StartZ=0 EndX=371.073 EndY=76.4095 EndZ=0
    g344: LineSegment StartX=318.073 StartY=72.4095 StartZ=0 EndX=318.073 EndY=-47.4805 EndZ=0
    g345: LineSegment StartX=375.073 StartY=72.4095 StartZ=0 EndX=375.073 EndY=-78.7896 EndZ=0
    g346: ArcOfCircle CenterX=-26.9272 CenterY=22.1087 CenterZ=0 NormalX=0 NormalY=0 NormalZ=1 AngleXU=0 Radius=4 StartAngle=5e-16 EndAngle=3.14159
    g347: LineSegment StartX=-30.9272 StartY=22.1087 StartZ=0 EndX=-34.9272 EndY=-83.7794 EndZ=0
    g348: LineSegment StartX=-18.9272 StartY=-83.7794 StartZ=0 EndX=-22.9272 EndY=22.1087 EndZ=0
  constraints (572):
    c: Coincident(g0,g2)
    c: Block(g0)
    c: Block(g1)
    c: Vertical(g3)
    c: Vertical(g4)
    c: Block(g4)
    c: Block(g3)
    c: Tangent(g6,g7) = 1.5708
    c: Tangent(g7,g9) = 1.5708
    c: Equal(g6,g9)
    c: Coincident(g8,g6)
    c: Coincident(g8,g9)
    c: Block(g7)
    c: Block(g8)
    c: Weight(g10) = 1
    c: Equal(g10,g11)
    c: Equal(g10,g12)
    c: InternalAlignment(g10,g13)
    c: InternalAlignment(g11,g13)
    c: InternalAlignment(g12,g13)
    c: InternalAlignment(g14,g13)
    c: InternalAlignment(g15,g13)
    c: Weight(g16) = 1
    c: Equal(g16,g17)
    c: Equal(g16,g18)
    c: InternalAlignment(g16,g19)
    c: InternalAlignment(g17,g19)
    c: InternalAlignment(g18,g19)
    c: InternalAlignment(g20,g19)
    c: InternalAlignment(g21,g19)
    c: Block(g19)
    c: Block(g13)
    c: Weight(g22) = 1
    c: Equal(g22,g23)
    c: Equal(g22,g24)
    c: InternalAlignment(g22,g25)
    c: InternalAlignment(g23,g25)
    c: InternalAlignment(g24,g25)
    c: InternalAlignment(g26,g25)
    c: InternalAlignment(g27,g25)
    c: Weight(g28) = 1
    c: Equal(g28,g29)
    c: Equal(g28,g30)
    c: InternalAlignment(g28,g31)
    c: InternalAlignment(g29,g31)
    c: InternalAlignment(g30,g31)
    c: InternalAlignment(g32,g31)
    c: InternalAlignment(g33,g31)
    c: Block(g31)
    c: Block(g25)
    c: Weight(g34) = 1
    c: Equal(g34,g35)
    c: Equal(g34,g36)
    c: InternalAlignment(g34,g37)
    c: InternalAlignment(g35,g37)
    c: InternalAlignment(g36,g37)
    c: InternalAlignment(g38,g37)
    c: InternalAlignment(g39,g37)
    c: Weight(g40) = 1
    c: Equal(g40,g41)
    c: Equal(g40,g42)
    c: InternalAlignment(g40,g43)
    c: InternalAlignment(g41,g43)
    c: InternalAlignment(g42,g43)
    c: InternalAlignment(g44,g43)
    c: InternalAlignment(g45,g43)
    c: Block(g37)
    c: Block(g43)
    c: Coincident(g46,g4)
    c: Coincident(g46,g3)
    c: Horizontal(g46)
    c: Distance(g46) = 450
    c: Coincident(g47,g4)
    c: Coincident(g47,g3)
    c: Horizontal(g47)
    c: Horizontal(g48)
    c: Coincident(g2,g48)
    c: Block(g48)
    c: Coincident(g1,g48)
    c: Weight(g49) = 1
    c: Equal(g49,g50)
    c: Equal(g49,g51)
    c: InternalAlignment(g49,g52)
    c: InternalAlignment(g50,g52)
    c: InternalAlignment(g51,g52)
    c: InternalAlignment(g53,g52)
    c: InternalAlignment(g54,g52)
    c: Block(g52)
    c: Weight(g55) = 1
    c: Equal(g55,g56)
    c: Equal(g55,g57)
    c: InternalAlignment(g55,g58)
    c: InternalAlignment(g56,g58)
    c: InternalAlignment(g57,g58)
    c: InternalAlignment(g59,g58)
    c: InternalAlignment(g60,g58)
    c: Block(g58)
    c: Weight(g61) = 1
    c: Equal(g61,g62)
    c: Equal(g61,g63)
    c: InternalAlignment(g61,g64)
    c: InternalAlignment(g62,g64)
    c: InternalAlignment(g63,g64)
    c: InternalAlignment(g65,g64)
    c: InternalAlignment(g66,g64)
    c: Block(g64)
    c: Weight(g67) = 1
    c: Equal(g67,g68)
    c: Equal(g67,g69)
    c: InternalAlignment(g67,g70)
    c: InternalAlignment(g68,g70)
    c: InternalAlignment(g69,g70)
    c: InternalAlignment(g71,g70)
    c: InternalAlignment(g72,g70)
    c: Block(g70)
    c: Weight(g73) = 1
    c: Equal(g73,g74)
    c: Equal(g73,g75)
    c: InternalAlignment(g73,g76)
    c: InternalAlignment(g74,g76)
    c: InternalAlignment(g75,g76)
    c: InternalAlignment(g77,g76)
    c: InternalAlignment(g78,g76)
    c: Weight(g79) = 1
    c: Equal(g79,g80)
    c: Equal(g79,g81)
    c: InternalAlignment(g79,g82)
    c: InternalAlignment(g80,g82)
    c: InternalAlignment(g81,g82)
    c: InternalAlignment(g83,g82)
    c: InternalAlignment(g84,g82)
    c: Block(g76)
    c: Block(g82)
    c: Coincident(g85,g76)
    c: Coincident(g85,g82)
    c: Vertical(g85)
    c: Coincident(g86,g76)
    c: Coincident(g86,g58)
    c: Coincident(g87,g58)
    c: Coincident(g87,g82)
    c: Weight(g88) = 1
    c: Equal(g88,g89)
    c: Equal(g88,g90)
    c: InternalAlignment(g88,g91)
    c: InternalAlignment(g89,g91)
    c: InternalAlignment(g90,g91)
    c: InternalAlignment(g92,g91)
    c: InternalAlignment(g93,g91)
    c: Weight(g94) = 1
    c: Equal(g94,g95)
    c: Equal(g94,g96)
    c: InternalAlignment(g94,g97)
    c: InternalAlignment(g95,g97)
    c: InternalAlignment(g96,g97)
    c: InternalAlignment(g98,g97)
    c: InternalAlignment(g99,g97)
    c: Block(g91)
    c: Block(g97)
    c: Coincident(g100,g91)
    c: Coincident(g100,g97)
    c: Vertical(g100)
    c: Coincident(g101,g91)
    c: Coincident(g101,g52)
    c: Coincident(g102,g52)
    c: Coincident(g102,g97)
    c: Weight(g103) = 1
    c: Equal(g103,g104)
    c: Equal(g103,g105)
    c: InternalAlignment(g103,g106)
    c: InternalAlignment(g104,g106)
    c: InternalAlignment(g105,g106)
    c: InternalAlignment(g107,g106)
    c: InternalAlignment(g108,g106)
    c: Weight(g109) = 1
    c: Equal(g109,g110)
    c: Equal(g109,g111)
    c: InternalAlignment(g109,g112)
    c: InternalAlignment(g110,g112)
    c: InternalAlignment(g111,g112)
    c: InternalAlignment(g113,g112)
    c: InternalAlignment(g114,g112)
    c: Block(g106)
    c: Block(g112)
    c: Coincident(g115,g106)
    c: Coincident(g115,g112)
    c: Vertical(g115)
    c: Coincident(g116,g112)
    c: Coincident(g116,g70)
    c: Coincident(g117,g70)
    c: Coincident(g117,g106)
    c: Weight(g118) = 1
    c: Equal(g118,g119)
    c: Equal(g118,g120)
    c: InternalAlignment(g118,g121)
    c: InternalAlignment(g119,g121)
    c: InternalAlignment(g120,g121)
    c: InternalAlignment(g122,g121)
    c: InternalAlignment(g123,g121)
    c: Weight(g124) = 1
    c: Equal(g124,g125)
    c: Equal(g124,g126)
    c: InternalAlignment(g124,g127)
    c: InternalAlignment(g125,g127)
    c: InternalAlignment(g126,g127)
    c: InternalAlignment(g128,g127)
    c: InternalAlignment(g129,g127)
    c: Block(g121)
    c: Block(g127)
    c: Coincident(g130,g121)
    c: Coincident(g130,g127)
    c: Vertical(g130)
    c: Coincident(g131,g127)
    c: Coincident(g131,g64)
    c: Coincident(g132,g64)
    c: Coincident(g132,g121)
    c: Weight(g133) = 1
    c: Equal(g133,g134)
    c: Equal(g133,g135)
    c: InternalAlignment(g133,g136)
    c: InternalAlignment(g134,g136)
    c: InternalAlignment(g135,g136)
    c: InternalAlignment(g137,g136)
    c: InternalAlignment(g138,g136)
    c: Weight(g139) = 1
    c: Equal(g139,g140)
    c: Equal(g139,g141)
    c: InternalAlignment(g139,g142)
    c: InternalAlignment(g140,g142)
    c: InternalAlignment(g141,g142)
    c: InternalAlignment(g143,g142)
    c: InternalAlignment(g144,g142)
    c: Weight(g145) = 1
    c: Equal(g145,g146)
    c: Equal(g145,g147)
    c: InternalAlignment(g145,g148)
    c: InternalAlignment(g146,g148)
    c: InternalAlignment(g147,g148)
    c: InternalAlignment(g149,g148)
    c: InternalAlignment(g150,g148)
    c: Weight(g151) = 1
    c: Equal(g151,g152)
    c: Equal(g151,g153)
    c: InternalAlignment(g151,g154)
    c: InternalAlignment(g152,g154)
    c: InternalAlignment(g153,g154)
    c: InternalAlignment(g155,g154)
    c: InternalAlignment(g156,g154)
    c: Block(g154)
    c: Block(g148)
    c: Block(g142)
    c: Block(g136)
    c: Coincident(g157,g31)
    c: Coincident(g157,g154)
    c: Coincident(g158,g154)
    c: Coincident(g158,g148)
    c: Horizontal(g158)
    c: Coincident(g159,g148)
    c: Coincident(g159,g31)
    c: Vertical(g159)
    c: Coincident(g160,g25)
    c: Coincident(g160,g142)
    c: Vertical(g160)
    c: Coincident(g161,g142)
    c: Coincident(g161,g136)
    c: Horizontal(g161)
    c: Coincident(g162,g136)
    c: Coincident(g162,g25)
    c: Weight(g163) = 1
    c: Equal(g163,g164)
    c: Equal(g163,g165)
    c: InternalAlignment(g163,g166)
    c: InternalAlignment(g164,g166)
    c: InternalAlignment(g165,g166)
    c: InternalAlignment(g167,g166)
    c: InternalAlignment(g168,g166)
    c: Weight(g169) = 1
    c: Equal(g169,g170)
    c: Equal(g169,g171)
    c: InternalAlignment(g169,g172)
    c: InternalAlignment(g170,g172)
    c: InternalAlignment(g171,g172)
    c: InternalAlignment(g173,g172)
    c: InternalAlignment(g174,g172)
    c: Weight(g175) = 1
    c: Equal(g175,g176)
    c: Equal(g175,g177)
    c: InternalAlignment(g175,g178)
    c: InternalAlignment(g176,g178)
    c: InternalAlignment(g177,g178)
    c: InternalAlignment(g179,g178)
    c: InternalAlignment(g180,g178)
    c: Weight(g181) = 1
    c: Equal(g181,g182)
    c: Equal(g181,g183)
    c: InternalAlignment(g181,g184)
    c: InternalAlignment(g182,g184)
    c: InternalAlignment(g183,g184)
    c: InternalAlignment(g185,g184)
    c: InternalAlignment(g186,g184)
    c: Block(g184)
    c: Block(g178)
    c: Block(g172)
    c: Block(g166)
    c: Coincident(g187,g184)
    c: Coincident(g187,g178)
    c: Horizontal(g187)
    c: Coincident(g188,g178)
    c: Coincident(g188,g13)
    c: Vertical(g188)
    c: Coincident(g189,g19)
    c: Coincident(g189,g172)
    c: Vertical(g189)
    c: Coincident(g190,g172)
    c: Coincident(g190,g166)
    c: Horizontal(g190)
    c: Coincident(g191,g166)
    c: Coincident(g191,g19)
    c: Coincident(g192,g13)
    c: Weight(g193) = 1
    c: Equal(g193,g194)
    c: Equal(g193,g195)
    c: InternalAlignment(g193,g196)
    c: InternalAlignment(g194,g196)
    c: InternalAlignment(g195,g196)
    c: InternalAlignment(g197,g196)
    c: InternalAlignment(g198,g196)
    c: Weight(g199) = 1
    c: Equal(g199,g200)
    c: Equal(g199,g201)
    c: InternalAlignment(g199,g202)
    c: InternalAlignment(g200,g202)
    c: InternalAlignment(g201,g202)
    c: InternalAlignment(g203,g202)
    c: InternalAlignment(g204,g202)
    c: Block(g202)
    c: Block(g196)
    c: Coincident(g205,g202)
    c: Coincident(g205,g37)
    c: Coincident(g206,g37)
    c: Coincident(g206,g196)
    c: Coincident(g207,g196)
    c: Coincident(g207,g202)
    c: Vertical(g207)
    c: Weight(g208) = 1
    c: Equal(g208,g209)
    c: Equal(g208,g210)
    c: InternalAlignment(g208,g211)
    c: InternalAlignment(g209,g211)
    c: InternalAlignment(g210,g211)
    c: InternalAlignment(g212,g211)
    c: InternalAlignment(g213,g211)
    c: Weight(g214) = 1
    c: Equal(g214,g215)
    c: Equal(g214,g216)
    c: InternalAlignment(g214,g217)
    c: InternalAlignment(g215,g217)
    c: InternalAlignment(g216,g217)
    c: InternalAlignment(g218,g217)
    c: InternalAlignment(g219,g217)
    c: Block(g217)
    c: Block(g211)
    c: Coincident(g220,g211)
    c: Coincident(g220,g43)
    c: Coincident(g221,g43)
    c: Coincident(g221,g217)
    c: Coincident(g222,g217)
    c: Coincident(g222,g211)
    c: Vertical(g222)
    c: Horizontal(g223)
    c: Block(g223)
    c: Vertical(g224)
    c: Block(g224)
    c: Block(g225)
    c: Weight(g226) = 1
    c: Equal(g226,g227)
    c: Equal(g226,g228)
    c: InternalAlignment(g226,g229)
    c: InternalAlignment(g227,g229)
    c: InternalAlignment(g228,g229)
    c: InternalAlignment(g230,g229)
    c: InternalAlignment(g231,g229)
    c: Weight(g232) = 1
    c: Equal(g232,g233)
    c: Equal(g232,g234)
    c: InternalAlignment(g232,g235)
    c: InternalAlignment(g233,g235)
    c: InternalAlignment(g234,g235)
    c: InternalAlignment(g236,g235)
    c: InternalAlignment(g237,g235)
    c: Weight(g238) = 1
    c: Equal(g238,g239)
    c: Equal(g238,g240)
    c: InternalAlignment(g238,g241)
    c: InternalAlignment(g239,g241)
    c: InternalAlignment(g240,g241)
    c: InternalAlignment(g242,g241)
    c: InternalAlignment(g243,g241)
    c: Weight(g244) = 1
    c: Equal(g244,g245)
    c: Equal(g244,g246)
    c: InternalAlignment(g244,g247)
    c: InternalAlignment(g245,g247)
    c: InternalAlignment(g246,g247)
    c: InternalAlignment(g248,g247)
    c: InternalAlignment(g249,g247)
    c: Block(g229)
    c: Block(g235)
    c: Block(g241)
    c: Block(g247)
    c: Coincident(g250,g235)
    c: Coincident(g250,g229)
    c: Horizontal(g250)
    c: Block(g192)
    c: Weight(g251) = 1
    c: Equal(g251,g252)
    c: Equal(g251,g253)
    c: InternalAlignment(g251,g254)
    c: InternalAlignment(g252,g254)
    c: InternalAlignment(g253,g254)
    c: InternalAlignment(g255,g254)
    c: InternalAlignment(g256,g254)
    c: Weight(g257) = 1
    c: Equal(g257,g258)
    c: Equal(g257,g259)
    c: InternalAlignment(g257,g260)
    c: InternalAlignment(g258,g260)
    c: InternalAlignment(g259,g260)
    c: InternalAlignment(g261,g260)
    c: InternalAlignment(g262,g260)
    c: Block(g254)
    c: Block(g260)
    c: Coincident(g263,g254)
    c: Coincident(g263,g260)
    c: Weight(g264) = 1
    c: Equal(g264,g265)
    c: Equal(g264,g266)
    c: InternalAlignment(g264,g267)
    c: InternalAlignment(g265,g267)
    c: InternalAlignment(g266,g267)
    c: InternalAlignment(g268,g267)
    c: InternalAlignment(g269,g267)
    c: Weight(g270) = 1
    c: Equal(g270,g271)
    c: Equal(g270,g272)
    c: InternalAlignment(g270,g273)
    c: InternalAlignment(g271,g273)
    c: InternalAlignment(g272,g273)
    c: InternalAlignment(g274,g273)
    c: InternalAlignment(g275,g273)
    c: Weight(g276) = 1
    c: Equal(g276,g277)
    c: Equal(g276,g278)
    c: InternalAlignment(g276,g279)
    c: InternalAlignment(g277,g279)
    c: InternalAlignment(g278,g279)
    c: InternalAlignment(g280,g279)
    c: InternalAlignment(g281,g279)
    c: Block(g279)
    c: Block(g273)
    c: Block(g267)
    c: Coincident(g282,g273)
    c: Coincident(g282,g267)
    c: Coincident(g283,g267)
    c: Coincident(g283,g279)
    c: Vertical(g283)
    c: Coincident(g284,g279)
    c: Coincident(g284,g273)
    c: Horizontal(g284)
    c: Weight(g285) = 1
    c: Equal(g285,g286)
    c: InternalAlignment(g285,g287)
    c: InternalAlignment(g286,g287)
    c: InternalAlignment(g288,g287)
    c: InternalAlignment(g289,g287)
    c: Weight(g290) = 1
    c: InternalAlignment(g291,g293)
    c: InternalAlignment(g292,g293)
    c: InternalAlignment(g294,g293)
    c: InternalAlignment(g295,g293)
    c: Weight(g296) = 1
    c: Equal(g296,g297)
    c: Equal(g296,g298)
    c: InternalAlignment(g296,g299)
    c: InternalAlignment(g297,g299)
    c: InternalAlignment(g298,g299)
    c: InternalAlignment(g300,g299)
    c: InternalAlignment(g301,g299)
    c: Equal(g302,g303)
    c: Equal(g302,g304)
    c: InternalAlignment(g302,g305)
    c: InternalAlignment(g303,g305)
    c: InternalAlignment(g304,g305)
    c: InternalAlignment(g306,g305)
    c: InternalAlignment(g307,g305)
    c: Block(g293)
    c: Block(g299)
    c: Block(g305)
    c: Block(g287)
    c: Coincident(g308,g287)
    c: Coincident(g308,g293)
    c: Horizontal(g308)
    c: Coincident(g309,g293)
    c: Coincident(g309,g299)
    c: Vertical(g309)
    c: Coincident(g310,g299)
    c: Coincident(g310,g305)
    c: Horizontal(g310)
    c: Coincident(g311,g305)
    c: Coincident(g311,g287)
    c: Weight(g312) = 1
    c: Equal(g312,g313)
    c: Equal(g312,g314)
    c: InternalAlignment(g312,g315)
    c: InternalAlignment(g313,g315)
    c: InternalAlignment(g314,g315)
    c: InternalAlignment(g316,g315)
    c: InternalAlignment(g317,g315)
    c: Weight(g318) = 1
    c: Equal(g318,g319)
    c: Equal(g318,g320)
    c: InternalAlignment(g318,g321)
    c: InternalAlignment(g319,g321)
    c: InternalAlignment(g320,g321)
    c: InternalAlignment(g322,g321)
    c: InternalAlignment(g323,g321)
    c: Weight(g324) = 1
    c: Equal(g324,g325)
    c: Equal(g324,g326)
    c: InternalAlignment(g324,g327)
    c: InternalAlignment(g325,g327)
    c: InternalAlignment(g326,g327)
    c: InternalAlignment(g328,g327)
    c: InternalAlignment(g329,g327)
    c: Block(g327)
    c: Block(g321)
    c: Block(g315)
    c: Coincident(g330,g327)
    c: Coincident(g330,g321)
    c: Horizontal(g330)
    c: Coincident(g331,g321)
    c: Coincident(g331,g315)
    c: Vertical(g331)
    c: Coincident(g332,g315)
    c: Coincident(g332,g327)
    c: InternalAlignment(g333,g334)
    c: InternalAlignment(g335,g334)
    c: InternalAlignment(g336,g334)
    c: Block(g334)
    c: Equal(g337,g338)
    c: Equal(g337,g339)
    c: InternalAlignment(g337,g340)
    c: InternalAlignment(g338,g340)
    c: InternalAlignment(g339,g340)
    c: InternalAlignment(g341,g340)
    c: InternalAlignment(g342,g340)
    c: Block(g340)
    c: Coincident(g343,g334)
    c: Horizontal(g343)
    c: Block(g343)
    c: Coincident(g344,g334)
    c: Coincident(g344,g260)
    c: Vertical(g344)
    c: Coincident(g345,g340)
    c: Coincident(g345,g254)
    c: Vertical(g345)
    c: Coincident(g347,g5)
    c: Coincident(g348,g5)
    c: Block(g346)
    c: Block(g5)
    c: Block(g348)
    c: Block(g347)
    c: Distance(g344) = 119.89
FEATURE [Sketcher::SketchObject] Sketch001
  FullyConstrained = true
  MapMode = 4
  Placement = pos=(0,0,0) rot=(0.57735,0.57735,0.57735;2.0944rad)
  Support = -> [Sketch]
  sketch-geometry (46):
    g0: BSplineCurve PolesCount=3 KnotsCount=2 Degree=2 IsPeriodic=0
    g1: ArcOfCircle CenterX=73.1223 CenterY=-32.291 CenterZ=0 NormalX=0 NormalY=0 NormalZ=1 AngleXU=0 Radius=13 StartAngle=5.92268 EndAngle=9.06428
    g2: ArcOfCircle CenterX=66.7816 CenterY=-49.1439 CenterZ=0 NormalX=0 NormalY=0 NormalZ=1 AngleXU=0 Radius=13 StartAngle=2.78068 EndAngle=5.92131
    g3: ArcOfCircle CenterX=55.9263 CenterY=-78.1807 CenterZ=0 NormalX=0 NormalY=0 NormalZ=1 AngleXU=0 Radius=13 StartAngle=5.92268 EndAngle=9.06428
    g4: ArcOfCircle CenterX=49.5884 CenterY=-95.0342 CenterZ=0 NormalX=0 NormalY=0 NormalZ=1 AngleXU=0 Radius=13 StartAngle=2.78068 EndAngle=5.92131
    g5: ArcOfCircle CenterX=38.7206 CenterY=-124.067 CenterZ=0 NormalX=0 NormalY=0 NormalZ=1 AngleXU=0 Radius=13 StartAngle=5.92268 EndAngle=9.06428
    g6: ArcOfCircle CenterX=32.3875 CenterY=-140.92 CenterZ=0 NormalX=0 NormalY=0 NormalZ=1 AngleXU=0 Radius=13 StartAngle=2.78068 EndAngle=5.92131
    g7: ArcOfCircle CenterX=21.4715 CenterY=-169.934 CenterZ=0 NormalX=0 NormalY=0 NormalZ=1 AngleXU=0 Radius=13 StartAngle=5.92268 EndAngle=9.06428
    g8: ArcOfCircle CenterX=15.1336 CenterY=-186.787 CenterZ=0 NormalX=0 NormalY=0 NormalZ=1 AngleXU=0 Radius=13 StartAngle=2.78068 EndAngle=5.92131
    g9-g12: Circle x4 (B-spline internal-alignment scaffolding for g13; pole/knot coordinates omitted)
    g13: BSplineCurve PolesCount=4 KnotsCount=2 Degree=3 IsPeriodic=0
    g14: GeomPoint X=28.8094 Y=-19.0875 Z=0
    g15: GeomPoint X=47.0443 Y=-50.4712 Z=0
    g16: Circle CenterX=53.5586 CenterY=-23.2695 CenterZ=0 NormalX=0 NormalY=0 NormalZ=1 AngleXU=0 Radius=3.24518
    g17: Circle CenterX=-195.441 CenterY=-127.082 CenterZ=0 NormalX=0 NormalY=0 NormalZ=1 AngleXU=0 Radius=1
    g18: Circle CenterX=-8.24091 CenterY=-197.481 CenterZ=0 NormalX=0 NormalY=0 NormalZ=1 AngleXU=0 Radius=1
    g19: Circle CenterX=12.8789 CenterY=-141.321 CenterZ=0 NormalX=0 NormalY=0 NormalZ=1 AngleXU=0 Radius=1
    g20: BSplineCurve PolesCount=3 KnotsCount=2 Degree=2 IsPeriodic=0
    g21: GeomPoint X=-195.441 Y=-127.082 Z=0
    g22: GeomPoint X=12.8789 Y=-141.321 Z=0
    g23: Circle CenterX=-12.8016 CenterY=-179.036 CenterZ=0 NormalX=0 NormalY=0 NormalZ=1 AngleXU=0 Radius=10.5072
    g24: Circle CenterX=0.933922 CenterY=-166.43 CenterZ=0 NormalX=0 NormalY=0 NormalZ=1 AngleXU=0 Radius=3.26661
    g25: Circle CenterX=-33.5518 CenterY=-176.44 CenterZ=0 NormalX=0 NormalY=0 NormalZ=1 AngleXU=0 Radius=5.64388
    g26: Circle CenterX=-47.2366 CenterY=-173.859 CenterZ=0 NormalX=0 NormalY=0 NormalZ=1 AngleXU=0 Radius=3.01653
    g27: Circle CenterX=-56.2595 CenterY=-171.456 CenterZ=0 NormalX=0 NormalY=0 NormalZ=1 AngleXU=0 Radius=2.12826
    g28: ArcOfCircle CenterX=51.2151 CenterY=-198.473 CenterZ=0 NormalX=0 NormalY=0 NormalZ=1 AngleXU=0 Radius=20 StartAngle=2.78189 EndAngle=4.35269
    g29: LineSegment StartX=32.4951 StartY=-191.433 StartZ=0 EndX=94.6578 EndY=-26.1352 EndZ=0
    g30: LineSegment StartX=43.1192 StartY=-220.001 StartZ=0 EndX=-196.497 EndY=-129.89 EndZ=0
    g31: LineSegment StartX=43.1192 StartY=-220.001 StartZ=0 EndX=44.1752 EndY=-217.193 EndZ=0
    g32: LineSegment StartX=117.223 StartY=-19.0875 StartZ=0 EndX=117.223 EndY=-16.0875 EndZ=0
    g33: LineSegment StartX=117.223 StartY=-16.0875 StartZ=0 EndX=17.2232 EndY=-16.0875 EndZ=0
    g34: LineSegment StartX=17.2232 StartY=-16.0875 StartZ=0 EndX=17.2232 EndY=-19.0875 EndZ=0
    g35: LineSegment StartX=28.8094 StartY=-19.0875 StartZ=0 EndX=17.2232 EndY=-19.0875 EndZ=0
    g36: LineSegment StartX=47.0443 StartY=-50.4712 StartZ=0 EndX=12.8789 EndY=-141.321 EndZ=0
    g37: LineSegment StartX=-195.441 StartY=-127.082 StartZ=0 EndX=-196.497 EndY=-129.89 EndZ=0
    g38: LineSegment StartX=85.2866 StartY=-36.8766 StartZ=0 EndX=78.9396 EndY=-53.7463 EndZ=0
    g39: LineSegment StartX=60.9579 StartY=-27.7053 StartZ=0 EndX=54.6191 EndY=-44.5532 EndZ=0
    g40: LineSegment StartX=68.0907 StartY=-82.7664 StartZ=0 EndX=61.7465 EndY=-99.6365 EndZ=0
    g41: LineSegment StartX=43.7619 StartY=-73.595 StartZ=0 EndX=37.426 EndY=-90.4435 EndZ=0
    g42: LineSegment StartX=50.885 StartY=-128.652 StartZ=0 EndX=44.5456 EndY=-145.522 EndZ=0
    g43: LineSegment StartX=26.5562 StartY=-119.481 StartZ=0 EndX=20.2251 EndY=-136.329 EndZ=0
    g44: LineSegment StartX=9.3071 StartY=-165.349 StartZ=0 EndX=2.97115 EndY=-182.197 EndZ=0
    g45: LineSegment StartX=33.6358 StartY=-174.52 StartZ=0 EndX=27.2917 EndY=-191.39 EndZ=0
  constraints (71):
    c: Block(g0)
    c: Block(g1)
    c: Block(g2)
    c: Block(g4)
    c: Block(g3)
    c: Block(g6)
    c: Block(g5)
    c: Block(g8)
    c: Block(g7)
    c: Weight(g9) = 1
    c: Equal(g9,g10)
    c: Equal(g9,g11)
    c: Equal(g9,g12)
    c: InternalAlignment(g9-g12 -> g13) x4
    c: InternalAlignment(g14,g13)
    c: InternalAlignment(g15,g13)
    c: Block(g16)
    c: Weight(g17) = 1
    c: Equal(g17,g18)
    c: Equal(g17,g19)
    c: InternalAlignment(g17,g20)
    c: InternalAlignment(g18,g20)
    c: InternalAlignment(g19,g20)
    c: InternalAlignment(g21,g20)
    c: InternalAlignment(g22,g20)
    c: Block(g20)
    c: Block(g23)
    c: Block(g24)
    c: Block(g25)
    c: Block(g26)
    c: Block(g27)
    c: Block(g28)
    c: Coincident(g29,g28)
    c: Coincident(g29,g0)
    c: Block(g13)
    c: Coincident(g31,g30)
    c: Coincident(g31,g28)
    c: Block(g31)
    c: Coincident(g32,g0)
    c: Vertical(g32)
    c: Coincident(g33,g32)
    c: Horizontal(g33)
    c: Coincident(g34,g33)
    c: Vertical(g34)
    c: Block(g33)
    c: Coincident(g35,g13)
    c: Coincident(g35,g34)
    c: Horizontal(g35)
    c: Coincident(g36,g13)
    c: Coincident(g36,g20)
    c: Coincident(g37,g20)
    c: Coincident(g37,g30)
    c: Block(g30)
    c: Coincident(g38,g1)
    c: Coincident(g38,g2)
    c: Coincident(g39,g1)
    c: Coincident(g39,g2)
    c: Coincident(g40,g3)
    c: Coincident(g40,g4)
    c: Coincident(g41,g3)
    c: Coincident(g41,g4)
    c: Coincident(g42,g5)
    c: Coincident(g42,g6)
    c: Coincident(g43,g5)
    c: Coincident(g43,g6)
    c: Coincident(g44,g7)
    c: Coincident(g44,g8)
    c: Coincident(g45,g7)
    c: Coincident(g45,g8)
    c: Distance(g30) = 256
    c: Distance(g33) = 100
FEATURE [Part::Extrusion] Extrude002
  Base = -> Sketch001
  Dir = (1,0,0)
  DirMode = 2
  FaceMakerClass = Part::FaceMakerBullseye
  LengthFwd = 8
  LengthRev = 0
  Solid = true
  Symmetric = false
FEATURE [Sketcher::SketchObject] Sketch002
  FullyConstrained = true
  sketch-geometry (20):
    g0: LineSegment StartX=-2.77179 StartY=-200.304 StartZ=0 EndX=5.22821 EndY=-200.304 EndZ=0
    g1: LineSegment StartX=5.22821 StartY=-200.304 StartZ=0 EndX=5.22821 EndY=-197.304 EndZ=0
    g2: LineSegment StartX=-2.77179 StartY=-200.304 StartZ=0 EndX=-2.77179 EndY=-197.304 EndZ=0
    g3: LineSegment StartX=5.22821 StartY=-197.304 StartZ=0 EndX=8.22821 EndY=-197.304 EndZ=0
    g4: LineSegment StartX=-2.77179 StartY=-197.304 StartZ=0 EndX=-5.77179 EndY=-197.304 EndZ=0
    g5: LineSegment StartX=19.2282 StartY=-203.304 StartZ=0 EndX=19.2282 EndY=-206.304 EndZ=0
    g6: LineSegment StartX=-16.7718 StartY=-203.304 StartZ=0 EndX=-16.7718 EndY=-206.304 EndZ=0
    g7: LineSegment StartX=-16.7718 StartY=-206.304 StartZ=0 EndX=19.2282 EndY=-206.304 EndZ=0
    g8: Circle CenterX=-16.7718 CenterY=-203.304 CenterZ=0 NormalX=0 NormalY=0 NormalZ=1 AngleXU=0 Radius=1
    g9: Circle CenterX=-5.77179 CenterY=-203.304 CenterZ=0 NormalX=0 NormalY=0 NormalZ=1 AngleXU=0 Radius=1
    g10: Circle CenterX=-5.77179 CenterY=-197.304 CenterZ=0 NormalX=0 NormalY=0 NormalZ=1 AngleXU=0 Radius=1
    g11: BSplineCurve PolesCount=3 KnotsCount=2 Degree=2 IsPeriodic=0
    g12: GeomPoint X=-16.7718 Y=-203.304 Z=0
    g13: GeomPoint X=-5.77179 Y=-197.304 Z=0
    g14: Circle CenterX=19.2282 CenterY=-203.304 CenterZ=0 NormalX=0 NormalY=0 NormalZ=1 AngleXU=0 Radius=1
    g15: Circle CenterX=8.22821 CenterY=-203.304 CenterZ=0 NormalX=0 NormalY=0 NormalZ=1 AngleXU=0 Radius=1
    g16: Circle CenterX=8.22821 CenterY=-197.304 CenterZ=0 NormalX=0 NormalY=0 NormalZ=1 AngleXU=0 Radius=1
    g17: BSplineCurve PolesCount=3 KnotsCount=2 Degree=2 IsPeriodic=0
    g18: GeomPoint X=19.2282 Y=-203.304 Z=0
    g19: GeomPoint X=8.22821 Y=-197.304 Z=0
  constraints (41):
    c: Horizontal(g0)
    c: Distance(g0) = 8
    c: Coincident(g1,g0)
    c: Vertical(g1)
    c: Distance(g1) = 3
    c: Coincident(g2,g0)
    c: Vertical(g2)
    c: Distance(g2) = 3
    c: Coincident(g3,g1)
    c: Horizontal(g3)
    c: Distance(g3) = 3
    c: Coincident(g4,g2)
    c: Horizontal(g4)
    c: Distance(g4) = 3
    c: Vertical(g5)
    c: Vertical(g6)
    c: Coincident(g7,g6)
    c: Coincident(g7,g5)
    c: Weight(g8) = 1
    c: Equal(g8,g9)
    c: Equal(g8,g10)
    c: Coincident(g11,g4)
    c: InternalAlignment(g8,g11)
    c: InternalAlignment(g9,g11)
    c: InternalAlignment(g10,g11)
    c: InternalAlignment(g12,g11)
    c: InternalAlignment(g13,g11)
    c: Coincident(g17,g5)
    c: Weight(g14) = 1
    c: Equal(g14,g15)
    c: Equal(g14,g16)
    c: Coincident(g17,g3)
    c: InternalAlignment(g14,g17)
    c: InternalAlignment(g15,g17)
    c: InternalAlignment(g16,g17)
    c: InternalAlignment(g18,g17)
    c: InternalAlignment(g19,g17)
    c: Block(g7)
    c: Block(g17)
    c: Block(g11)
    c: Block(g6)
FEATURE [Part::Extrusion] Extrude003
  Base = -> Sketch002
  Dir = (0,0,1)
  DirMode = 2
  FaceMakerClass = Part::FaceMakerBullseye
  LengthFwd = 260
  LengthRev = 0
  Solid = true
  Symmetric = false
FEATURE [Sketcher::SketchObject] Sketch003
  FullyConstrained = false
  sketch-geometry (400):
    g0: LineSegment StartX=-42.9272 StartY=136.221 StartZ=0 EndX=-42.9272 EndY=-103.779 EndZ=0
    g1: LineSegment StartX=407.073 StartY=136.221 StartZ=0 EndX=407.073 EndY=-103.779 EndZ=0
    g2: ArcOfCircle CenterX=-26.9272 CenterY=-83.7794 CenterZ=0 NormalX=0 NormalY=0 NormalZ=1 AngleXU=0 Radius=8 StartAngle=3.14159 EndAngle=6.28319
    g3: ArcOfCircle CenterX=391.073 CenterY=-83.7794 CenterZ=0 NormalX=0 NormalY=0 NormalZ=1 AngleXU=0 Radius=8 StartAngle=3.14159 EndAngle=6.28319
    g4: Circle CenterX=175.022 CenterY=27.0628 CenterZ=0 NormalX=0 NormalY=0 NormalZ=1 AngleXU=0 Radius=1
    g5: Circle CenterX=179.022 CenterY=24.8665 CenterZ=0 NormalX=0 NormalY=0 NormalZ=1 AngleXU=0 Radius=1
    g6: Circle CenterX=179.022 CenterY=27.0628 CenterZ=0 NormalX=0 NormalY=0 NormalZ=1 AngleXU=0 Radius=1
    g7: BSplineCurve PolesCount=3 KnotsCount=2 Degree=2 IsPeriodic=0
    g8: GeomPoint X=175.022 Y=27.0628 Z=0
    g9: GeomPoint X=179.022 Y=27.0628 Z=0
    g10: Circle CenterX=189.124 CenterY=27.0628 CenterZ=0 NormalX=0 NormalY=0 NormalZ=1 AngleXU=0 Radius=1
    g11: Circle CenterX=185.124 CenterY=24.8665 CenterZ=0 NormalX=0 NormalY=0 NormalZ=1 AngleXU=0 Radius=1
    g12: Circle CenterX=185.124 CenterY=27.0628 CenterZ=0 NormalX=0 NormalY=0 NormalZ=1 AngleXU=0 Radius=1
    g13: BSplineCurve PolesCount=3 KnotsCount=2 Degree=2 IsPeriodic=0
    g14: GeomPoint X=189.124 Y=27.0628 Z=0
    g15: GeomPoint X=185.124 Y=27.0628 Z=0
    g16: Circle CenterX=175.022 CenterY=5.37834 CenterZ=0 NormalX=0 NormalY=0 NormalZ=1 AngleXU=0 Radius=1
    g17: Circle CenterX=179.022 CenterY=7.57463 CenterZ=0 NormalX=0 NormalY=0 NormalZ=1 AngleXU=0 Radius=1
    g18: Circle CenterX=179.022 CenterY=5.34704 CenterZ=0 NormalX=0 NormalY=0 NormalZ=1 AngleXU=0 Radius=1
    g19: BSplineCurve PolesCount=3 KnotsCount=2 Degree=2 IsPeriodic=0
    g20: GeomPoint X=175.022 Y=5.37834 Z=0
    g21: GeomPoint X=179.022 Y=5.34704 Z=0
    g22: Circle CenterX=189.124 CenterY=5.37834 CenterZ=0 NormalX=0 NormalY=0 NormalZ=1 AngleXU=0 Radius=1
    g23: Circle CenterX=185.124 CenterY=7.57463 CenterZ=0 NormalX=0 NormalY=0 NormalZ=1 AngleXU=0 Radius=1
    g24: Circle CenterX=185.124 CenterY=5.34704 CenterZ=0 NormalX=0 NormalY=0 NormalZ=1 AngleXU=0 Radius=1
    g25: BSplineCurve PolesCount=3 KnotsCount=2 Degree=2 IsPeriodic=0
    g26: GeomPoint X=189.124 Y=5.37834 Z=0
    g27: GeomPoint X=185.124 Y=5.34704 Z=0
    g28: Circle CenterX=165.871 CenterY=18.1458 CenterZ=0 NormalX=0 NormalY=0 NormalZ=1 AngleXU=0 Radius=1
    g29: Circle CenterX=169.377 CenterY=16.2206 CenterZ=0 NormalX=0 NormalY=0 NormalZ=1 AngleXU=0 Radius=1
    g30: Circle CenterX=165.871 CenterY=14.2954 CenterZ=0 NormalX=0 NormalY=0 NormalZ=1 AngleXU=0 Radius=1
    g31: BSplineCurve PolesCount=3 KnotsCount=2 Degree=2 IsPeriodic=0
    g32: GeomPoint X=165.871 Y=18.1458 Z=0
    g33: GeomPoint X=165.871 Y=14.2954 Z=0
    g34: Circle CenterX=198.275 CenterY=18.1458 CenterZ=0 NormalX=0 NormalY=0 NormalZ=1 AngleXU=0 Radius=1
    g35: Circle CenterX=194.768 CenterY=16.2206 CenterZ=0 NormalX=0 NormalY=0 NormalZ=1 AngleXU=0 Radius=1
    g36: Circle CenterX=198.275 CenterY=14.2954 CenterZ=0 NormalX=0 NormalY=0 NormalZ=1 AngleXU=0 Radius=1
    g37: BSplineCurve PolesCount=3 KnotsCount=2 Degree=2 IsPeriodic=0
    g38: GeomPoint X=198.275 Y=18.1458 Z=0
    g39: GeomPoint X=198.275 Y=14.2954 Z=0
    g40: LineSegment StartX=407.073 StartY=-103.779 StartZ=0 EndX=-42.9272 EndY=-103.779 EndZ=0
    g41: Circle CenterX=125.607 CenterY=54.1951 CenterZ=0 NormalX=0 NormalY=0 NormalZ=1 AngleXU=0 Radius=1
    g42: Circle CenterX=139.632 CenterY=46.4944 CenterZ=0 NormalX=0 NormalY=0 NormalZ=1 AngleXU=0 Radius=1
    g43: Circle CenterX=127.326 CenterY=56.7187 CenterZ=0 NormalX=0 NormalY=0 NormalZ=1 AngleXU=0 Radius=1
    g44: BSplineCurve PolesCount=3 KnotsCount=2 Degree=2 IsPeriodic=0
    g45: GeomPoint X=125.607 Y=54.1951 Z=0
    g46: GeomPoint X=127.326 Y=56.7187 Z=0
    g47: Circle CenterX=236.821 CenterY=56.7187 CenterZ=0 NormalX=0 NormalY=0 NormalZ=1 AngleXU=0 Radius=1
    g48: Circle CenterX=224.513 CenterY=46.4944 CenterZ=0 NormalX=0 NormalY=0 NormalZ=1 AngleXU=0 Radius=1
    g49: Circle CenterX=238.538 CenterY=54.1951 CenterZ=0 NormalX=0 NormalY=0 NormalZ=1 AngleXU=0 Radius=1
    g50: BSplineCurve PolesCount=3 KnotsCount=2 Degree=2 IsPeriodic=0
    g51: GeomPoint X=236.821 Y=56.7187 Z=0
    g52: GeomPoint X=238.538 Y=54.1951 Z=0
    g53: Circle CenterX=238.538 CenterY=-21.7539 CenterZ=0 NormalX=0 NormalY=0 NormalZ=1 AngleXU=0 Radius=1
    g54: Circle CenterX=224.513 CenterY=-14.0532 CenterZ=0 NormalX=0 NormalY=0 NormalZ=1 AngleXU=0 Radius=1
    g55: Circle CenterX=236.821 CenterY=-24.2775 CenterZ=0 NormalX=0 NormalY=0 NormalZ=1 AngleXU=0 Radius=1
    g56: BSplineCurve PolesCount=3 KnotsCount=2 Degree=2 IsPeriodic=0
    g57: GeomPoint X=238.538 Y=-21.7539 Z=0
    g58: GeomPoint X=236.821 Y=-24.2775 Z=0
    g59: Circle CenterX=125.607 CenterY=-21.7539 CenterZ=0 NormalX=0 NormalY=0 NormalZ=1 AngleXU=0 Radius=1
    g60: Circle CenterX=139.632 CenterY=-14.0532 CenterZ=0 NormalX=0 NormalY=0 NormalZ=1 AngleXU=0 Radius=1
    g61: Circle CenterX=127.325 CenterY=-24.2775 CenterZ=0 NormalX=0 NormalY=0 NormalZ=1 AngleXU=0 Radius=1
    g62: BSplineCurve PolesCount=3 KnotsCount=2 Degree=2 IsPeriodic=0
    g63: GeomPoint X=125.607 Y=-21.7539 Z=0
    g64: GeomPoint X=127.325 Y=-24.2775 Z=0
    g65: Circle CenterX=302.996 CenterY=111.695 CenterZ=0 NormalX=0 NormalY=0 NormalZ=1 AngleXU=0 Radius=1
    g66: Circle CenterX=306.073 CenterY=114.251 CenterZ=0 NormalX=0 NormalY=0 NormalZ=1 AngleXU=0 Radius=1
    g67: Circle CenterX=306.073 CenterY=110.251 CenterZ=0 NormalX=0 NormalY=0 NormalZ=1 AngleXU=0 Radius=1
    g68: BSplineCurve PolesCount=3 KnotsCount=2 Degree=2 IsPeriodic=0
    g69: GeomPoint X=302.996 Y=111.695 Z=0
    g70: GeomPoint X=306.073 Y=110.251 Z=0
    g71: Circle CenterX=306.073 CenterY=95.2763 CenterZ=0 NormalX=0 NormalY=0 NormalZ=1 AngleXU=0 Radius=1
    g72: Circle CenterX=306.073 CenterY=91.2763 CenterZ=0 NormalX=0 NormalY=0 NormalZ=1 AngleXU=0 Radius=1
    g73: Circle CenterX=302.567 CenterY=89.3511 CenterZ=0 NormalX=0 NormalY=0 NormalZ=1 AngleXU=0 Radius=1
    g74: BSplineCurve PolesCount=3 KnotsCount=2 Degree=2 IsPeriodic=0
    g75: GeomPoint X=306.073 Y=95.2763 Z=0
    g76: GeomPoint X=302.567 Y=89.3511 Z=0
    g77: LineSegment StartX=306.073 StartY=110.251 StartZ=0 EndX=306.073 EndY=95.2763 EndZ=0
    g78: LineSegment StartX=302.996 StartY=111.695 StartZ=0 EndX=236.821 EndY=56.7187 EndZ=0
    g79: LineSegment StartX=238.538 StartY=54.1951 StartZ=0 EndX=302.567 EndY=89.3511 EndZ=0
    g80: Circle CenterX=61.1496 CenterY=111.695 CenterZ=0 NormalX=0 NormalY=0 NormalZ=1 AngleXU=0 Radius=1
    g81: Circle CenterX=58.0728 CenterY=114.251 CenterZ=0 NormalX=0 NormalY=0 NormalZ=1 AngleXU=0 Radius=1
    g82: Circle CenterX=58.0728 CenterY=110.251 CenterZ=0 NormalX=0 NormalY=0 NormalZ=1 AngleXU=0 Radius=1
    g83: BSplineCurve PolesCount=3 KnotsCount=2 Degree=2 IsPeriodic=0
    g84: GeomPoint X=61.1496 Y=111.695 Z=0
    g85: GeomPoint X=58.0728 Y=110.251 Z=0
    g86: Circle CenterX=61.5791 CenterY=89.3511 CenterZ=0 NormalX=0 NormalY=0 NormalZ=1 AngleXU=0 Radius=1
    g87: Circle CenterX=58.0728 CenterY=91.2763 CenterZ=0 NormalX=0 NormalY=0 NormalZ=1 AngleXU=0 Radius=1
    g88: Circle CenterX=58.0728 CenterY=95.2763 CenterZ=0 NormalX=0 NormalY=0 NormalZ=1 AngleXU=0 Radius=1
    g89: BSplineCurve PolesCount=3 KnotsCount=2 Degree=2 IsPeriodic=0
    g90: GeomPoint X=61.5791 Y=89.3511 Z=0
    g91: GeomPoint X=58.0728 Y=95.2763 Z=0
    g92: LineSegment StartX=58.0728 StartY=110.251 StartZ=0 EndX=58.0728 EndY=95.2763 EndZ=0
    g93: LineSegment StartX=61.1496 StartY=111.695 StartZ=0 EndX=127.326 EndY=56.7187 EndZ=0
    g94: LineSegment StartX=125.607 StartY=54.1951 StartZ=0 EndX=61.5791 EndY=89.3511 EndZ=0
    g95: Circle CenterX=61.5791 CenterY=-56.9099 CenterZ=0 NormalX=0 NormalY=0 NormalZ=1 AngleXU=0 Radius=1
    g96: Circle CenterX=58.0728 CenterY=-58.8351 CenterZ=0 NormalX=0 NormalY=0 NormalZ=1 AngleXU=0 Radius=1
    g97: Circle CenterX=58.0728 CenterY=-62.8351 CenterZ=0 NormalX=0 NormalY=0 NormalZ=1 AngleXU=0 Radius=1
    g98: BSplineCurve PolesCount=3 KnotsCount=2 Degree=2 IsPeriodic=0
    g99: GeomPoint X=61.5791 Y=-56.9099 Z=0
    g100: GeomPoint X=58.0728 Y=-62.8351 Z=0
    g101: Circle CenterX=58.0728 CenterY=-77.8102 CenterZ=0 NormalX=0 NormalY=0 NormalZ=1 AngleXU=0 Radius=1
    g102: Circle CenterX=58.0728 CenterY=-81.8102 CenterZ=0 NormalX=0 NormalY=0 NormalZ=1 AngleXU=0 Radius=1
    g103: Circle CenterX=61.1496 CenterY=-79.2541 CenterZ=0 NormalX=0 NormalY=0 NormalZ=1 AngleXU=0 Radius=1
    g104: BSplineCurve PolesCount=3 KnotsCount=2 Degree=2 IsPeriodic=0
    g105: GeomPoint X=58.0728 Y=-77.8102 Z=0
    g106: GeomPoint X=61.1496 Y=-79.2541 Z=0
    g107: LineSegment StartX=58.0728 StartY=-62.8351 StartZ=0 EndX=58.0728 EndY=-77.8102 EndZ=0
    g108: LineSegment StartX=61.1496 StartY=-79.2541 StartZ=0 EndX=127.325 EndY=-24.2775 EndZ=0
    g109: LineSegment StartX=125.607 StartY=-21.7539 StartZ=0 EndX=61.5791 EndY=-56.9099 EndZ=0
    g110: Circle CenterX=302.567 CenterY=-56.9099 CenterZ=0 NormalX=0 NormalY=0 NormalZ=1 AngleXU=0 Radius=1
    g111: Circle CenterX=306.073 CenterY=-58.8351 CenterZ=0 NormalX=0 NormalY=0 NormalZ=1 AngleXU=0 Radius=1
    g112: Circle CenterX=306.073 CenterY=-62.8351 CenterZ=0 NormalX=0 NormalY=0 NormalZ=1 AngleXU=0 Radius=1
    g113: BSplineCurve PolesCount=3 KnotsCount=2 Degree=2 IsPeriodic=0
    g114: GeomPoint X=302.567 Y=-56.9099 Z=0
    g115: GeomPoint X=306.073 Y=-62.8351 Z=0
    g116: Circle CenterX=302.996 CenterY=-79.2541 CenterZ=0 NormalX=0 NormalY=0 NormalZ=1 AngleXU=0 Radius=1
    g117: Circle CenterX=306.073 CenterY=-81.8102 CenterZ=0 NormalX=0 NormalY=0 NormalZ=1 AngleXU=0 Radius=1
    g118: Circle CenterX=306.073 CenterY=-77.8102 CenterZ=0 NormalX=0 NormalY=0 NormalZ=1 AngleXU=0 Radius=1
    g119: BSplineCurve PolesCount=3 KnotsCount=2 Degree=2 IsPeriodic=0
    g120: GeomPoint X=302.996 Y=-79.2541 Z=0
    g121: GeomPoint X=306.073 Y=-77.8102 Z=0
    g122: LineSegment StartX=306.073 StartY=-62.8351 StartZ=0 EndX=306.073 EndY=-77.8102 EndZ=0
    g123: LineSegment StartX=302.996 StartY=-79.2541 StartZ=0 EndX=236.821 EndY=-24.2775 EndZ=0
    g124: LineSegment StartX=238.538 StartY=-21.7539 StartZ=0 EndX=302.567 EndY=-56.9099 EndZ=0
    g125: Circle CenterX=61.6457 CenterY=-88.8112 CenterZ=0 NormalX=0 NormalY=0 NormalZ=1 AngleXU=0 Radius=1
    g126: Circle CenterX=58.0728 CenterY=-91.7794 CenterZ=0 NormalX=0 NormalY=0 NormalZ=1 AngleXU=0 Radius=1
    g127: Circle CenterX=63.9135 CenterY=-91.7794 CenterZ=0 NormalX=0 NormalY=0 NormalZ=1 AngleXU=0 Radius=1
    g128: BSplineCurve PolesCount=3 KnotsCount=2 Degree=2 IsPeriodic=0
    g129: GeomPoint X=61.6457 Y=-88.8112 Z=0
    g130: GeomPoint X=63.9135 Y=-91.7794 Z=0
    g131: Circle CenterX=179.022 CenterY=-85.8163 CenterZ=0 NormalX=0 NormalY=0 NormalZ=1 AngleXU=0 Radius=1
    g132: Circle CenterX=179.022 CenterY=-91.7794 CenterZ=0 NormalX=0 NormalY=0 NormalZ=1 AngleXU=0 Radius=1
    g133: Circle CenterX=171.895 CenterY=-91.7794 CenterZ=0 NormalX=0 NormalY=0 NormalZ=1 AngleXU=0 Radius=1
    g134: BSplineCurve PolesCount=3 KnotsCount=2 Degree=2 IsPeriodic=0
    g135: GeomPoint X=179.022 Y=-85.8163 Z=0
    g136: GeomPoint X=171.895 Y=-91.7794 Z=0
    g137: Circle CenterX=185.124 CenterY=-86.2028 CenterZ=0 NormalX=0 NormalY=0 NormalZ=1 AngleXU=0 Radius=1
    g138: Circle CenterX=185.124 CenterY=-91.7794 CenterZ=0 NormalX=0 NormalY=0 NormalZ=1 AngleXU=0 Radius=1
    g139: Circle CenterX=191.747 CenterY=-91.7794 CenterZ=0 NormalX=0 NormalY=0 NormalZ=1 AngleXU=0 Radius=1
    g140: BSplineCurve PolesCount=3 KnotsCount=2 Degree=2 IsPeriodic=0
    g141: GeomPoint X=185.124 Y=-86.2028 Z=0
    g142: GeomPoint X=191.747 Y=-91.7794 Z=0
    g143: Circle CenterX=299.888 CenterY=-86.6413 CenterZ=0 NormalX=0 NormalY=0 NormalZ=1 AngleXU=0 Radius=1
    g144: Circle CenterX=306.073 CenterY=-91.7794 CenterZ=0 NormalX=0 NormalY=0 NormalZ=1 AngleXU=0 Radius=1
    g145: Circle CenterX=298.776 CenterY=-91.7794 CenterZ=0 NormalX=0 NormalY=0 NormalZ=1 AngleXU=0 Radius=1
    g146: BSplineCurve PolesCount=3 KnotsCount=2 Degree=2 IsPeriodic=0
    g147: GeomPoint X=299.888 Y=-86.6413 Z=0
    g148: GeomPoint X=298.776 Y=-91.7794 Z=0
    g149: LineSegment StartX=189.124 StartY=5.37834 StartZ=0 EndX=299.888 EndY=-86.6413 EndZ=0
    g150: LineSegment StartX=298.776 StartY=-91.7794 StartZ=0 EndX=191.747 EndY=-91.7794 EndZ=0
    g151: LineSegment StartX=185.124 StartY=-86.2028 StartZ=0 EndX=185.124 EndY=5.34704 EndZ=0
    g152: LineSegment StartX=179.022 StartY=5.34704 StartZ=0 EndX=179.022 EndY=-85.8163 EndZ=0
    g153: LineSegment StartX=171.895 StartY=-91.7794 StartZ=0 EndX=63.9135 EndY=-91.7794 EndZ=0
    g154: LineSegment StartX=61.6457 StartY=-88.8112 StartZ=0 EndX=175.022 EndY=5.37834 EndZ=0
    g155: Circle CenterX=302.073 CenterY=124.221 CenterZ=0 NormalX=0 NormalY=0 NormalZ=1 AngleXU=0 Radius=1
    g156: Circle CenterX=306.073 CenterY=124.221 CenterZ=0 NormalX=0 NormalY=0 NormalZ=1 AngleXU=0 Radius=1
    g157: Circle CenterX=302.996 CenterY=121.665 CenterZ=0 NormalX=0 NormalY=0 NormalZ=1 AngleXU=0 Radius=1
    g158: BSplineCurve PolesCount=3 KnotsCount=2 Degree=2 IsPeriodic=0
    g159: GeomPoint X=302.073 Y=124.221 Z=0
    g160: GeomPoint X=302.996 Y=121.665 Z=0
    g161: Circle CenterX=189.124 CenterY=124.221 CenterZ=0 NormalX=0 NormalY=0 NormalZ=1 AngleXU=0 Radius=1
    g162: Circle CenterX=185.124 CenterY=124.221 CenterZ=0 NormalX=0 NormalY=0 NormalZ=1 AngleXU=0 Radius=1
    g163: Circle CenterX=185.124 CenterY=120.221 CenterZ=0 NormalX=0 NormalY=0 NormalZ=1 AngleXU=0 Radius=1
    g164: BSplineCurve PolesCount=3 KnotsCount=2 Degree=2 IsPeriodic=0
    g165: GeomPoint X=189.124 Y=124.221 Z=0
    g166: GeomPoint X=185.124 Y=120.221 Z=0
    g167: Circle CenterX=175.022 CenterY=124.221 CenterZ=0 NormalX=0 NormalY=0 NormalZ=1 AngleXU=0 Radius=1
    g168: Circle CenterX=179.022 CenterY=124.221 CenterZ=0 NormalX=0 NormalY=0 NormalZ=1 AngleXU=0 Radius=1
    g169: Circle CenterX=179.022 CenterY=120.221 CenterZ=0 NormalX=0 NormalY=0 NormalZ=1 AngleXU=0 Radius=1
    g170: BSplineCurve PolesCount=3 KnotsCount=2 Degree=2 IsPeriodic=0
    g171: GeomPoint X=175.022 Y=124.221 Z=0
    g172: GeomPoint X=179.022 Y=120.221 Z=0
    g173: Circle CenterX=62.0728 CenterY=124.221 CenterZ=0 NormalX=0 NormalY=0 NormalZ=1 AngleXU=0 Radius=1
    g174: Circle CenterX=58.0728 CenterY=124.221 CenterZ=0 NormalX=0 NormalY=0 NormalZ=1 AngleXU=0 Radius=1
    g175: Circle CenterX=61.1496 CenterY=121.665 CenterZ=0 NormalX=0 NormalY=0 NormalZ=1 AngleXU=0 Radius=1
    g176: BSplineCurve PolesCount=3 KnotsCount=2 Degree=2 IsPeriodic=0
    g177: GeomPoint X=62.0728 Y=124.221 Z=0
    g178: GeomPoint X=61.1496 Y=121.665 Z=0
    g179: LineSegment StartX=179.022 StartY=120.221 StartZ=0 EndX=179.022 EndY=27.0628 EndZ=0
    g180: LineSegment StartX=185.124 StartY=27.0628 StartZ=0 EndX=185.124 EndY=120.221 EndZ=0
    g181: LineSegment StartX=302.996 StartY=121.665 StartZ=0 EndX=189.124 EndY=27.0628 EndZ=0
    g182: LineSegment StartX=175.022 StartY=27.0628 StartZ=0 EndX=61.1496 EndY=121.665 EndZ=0
    g183: Circle CenterX=61.5791 CenterY=75.4095 CenterZ=0 NormalX=0 NormalY=0 NormalZ=1 AngleXU=0 Radius=1
    g184: Circle CenterX=58.0728 CenterY=77.3346 CenterZ=0 NormalX=0 NormalY=0 NormalZ=1 AngleXU=0 Radius=1
    g185: Circle CenterX=58.0728 CenterY=73.3346 CenterZ=0 NormalX=0 NormalY=0 NormalZ=1 AngleXU=0 Radius=1
    g186: BSplineCurve PolesCount=3 KnotsCount=2 Degree=2 IsPeriodic=0
    g187: GeomPoint X=61.5791 Y=75.4095 Z=0
    g188: GeomPoint X=58.0728 Y=73.3346 Z=0
    g189: Circle CenterX=58.0728 CenterY=-40.8935 CenterZ=0 NormalX=0 NormalY=0 NormalZ=1 AngleXU=0 Radius=1
    g190: Circle CenterX=58.0728 CenterY=-44.8935 CenterZ=0 NormalX=0 NormalY=0 NormalZ=1 AngleXU=0 Radius=1
    g191: Circle CenterX=61.5791 CenterY=-42.9683 CenterZ=0 NormalX=0 NormalY=0 NormalZ=1 AngleXU=0 Radius=1
    g192: BSplineCurve PolesCount=3 KnotsCount=2 Degree=2 IsPeriodic=0
    g193: GeomPoint X=58.0728 Y=-40.8935 Z=0
    g194: GeomPoint X=61.5791 Y=-42.9683 Z=0
    g195: LineSegment StartX=61.5791 StartY=-42.9683 StartZ=0 EndX=165.871 EndY=14.2954 EndZ=0
    g196: LineSegment StartX=165.871 StartY=18.1458 StartZ=0 EndX=61.5791 EndY=75.4095 EndZ=0
    g197: LineSegment StartX=58.0728 StartY=73.3346 StartZ=0 EndX=58.0728 EndY=-40.8935 EndZ=0
    g198: Circle CenterX=302.567 CenterY=-42.9683 CenterZ=0 NormalX=0 NormalY=0 NormalZ=1 AngleXU=0 Radius=1
    g199: Circle CenterX=306.073 CenterY=-44.8935 CenterZ=0 NormalX=0 NormalY=0 NormalZ=1 AngleXU=0 Radius=1
    g200: Circle CenterX=306.073 CenterY=-40.8935 CenterZ=0 NormalX=0 NormalY=0 NormalZ=1 AngleXU=0 Radius=1
    g201: BSplineCurve PolesCount=3 KnotsCount=2 Degree=2 IsPeriodic=0
    g202: GeomPoint X=302.567 Y=-42.9683 Z=0
    g203: GeomPoint X=306.073 Y=-40.8935 Z=0
    g204: Circle CenterX=306.073 CenterY=73.3346 CenterZ=0 NormalX=0 NormalY=0 NormalZ=1 AngleXU=0 Radius=1
    g205: Circle CenterX=306.073 CenterY=77.3346 CenterZ=0 NormalX=0 NormalY=0 NormalZ=1 AngleXU=0 Radius=1
    g206: Circle CenterX=302.567 CenterY=75.4095 CenterZ=0 NormalX=0 NormalY=0 NormalZ=1 AngleXU=0 Radius=1
    g207: BSplineCurve PolesCount=3 KnotsCount=2 Degree=2 IsPeriodic=0
    g208: GeomPoint X=306.073 Y=73.3346 Z=0
    g209: GeomPoint X=302.567 Y=75.4095 Z=0
    g210: LineSegment StartX=302.567 StartY=-42.9683 StartZ=0 EndX=198.275 EndY=14.2954 EndZ=0
    g211: LineSegment StartX=198.275 StartY=18.1458 StartZ=0 EndX=302.567 EndY=75.4095 EndZ=0
    g212: LineSegment StartX=306.073 StartY=73.3346 StartZ=0 EndX=306.073 EndY=-40.8935 EndZ=0
    g213: LineSegment StartX=322.073 StartY=105.865 StartZ=0 EndX=328.643 EndY=105.865 EndZ=0
    g214: LineSegment StartX=318.073 StartY=120.221 StartZ=0 EndX=318.073 EndY=109.865 EndZ=0
    g215: LineSegment StartX=336.157 StartY=107.779 StartZ=0 EndX=362.567 EndY=122.294 EndZ=0
    g216: Circle CenterX=362.073 CenterY=124.221 CenterZ=0 NormalX=0 NormalY=0 NormalZ=1 AngleXU=0 Radius=1
    g217: Circle CenterX=366.073 CenterY=124.221 CenterZ=0 NormalX=0 NormalY=0 NormalZ=1 AngleXU=0 Radius=1
    g218: Circle CenterX=362.567 CenterY=122.294 CenterZ=0 NormalX=0 NormalY=0 NormalZ=1 AngleXU=0 Radius=1
    g219: BSplineCurve PolesCount=3 KnotsCount=2 Degree=2 IsPeriodic=0
    g220: GeomPoint X=362.073 Y=124.221 Z=0
    g221: GeomPoint X=362.567 Y=122.294 Z=0
    g222: Circle CenterX=322.073 CenterY=124.221 CenterZ=0 NormalX=0 NormalY=0 NormalZ=1 AngleXU=0 Radius=1
    g223: Circle CenterX=318.073 CenterY=124.221 CenterZ=0 NormalX=0 NormalY=0 NormalZ=1 AngleXU=0 Radius=1
    g224: Circle CenterX=318.073 CenterY=120.221 CenterZ=0 NormalX=0 NormalY=0 NormalZ=1 AngleXU=0 Radius=1
    g225: BSplineCurve PolesCount=3 KnotsCount=2 Degree=2 IsPeriodic=0
    g226: GeomPoint X=322.073 Y=124.221 Z=0
    g227: GeomPoint X=318.073 Y=120.221 Z=0
    g228: Circle CenterX=322.073 CenterY=105.865 CenterZ=0 NormalX=0 NormalY=0 NormalZ=1 AngleXU=0 Radius=1
    g229: Circle CenterX=318.073 CenterY=105.865 CenterZ=0 NormalX=0 NormalY=0 NormalZ=1 AngleXU=0 Radius=1
    g230: Circle CenterX=318.073 CenterY=109.865 CenterZ=0 NormalX=0 NormalY=0 NormalZ=1 AngleXU=0 Radius=1
    g231: BSplineCurve PolesCount=3 KnotsCount=2 Degree=2 IsPeriodic=0
    g232: GeomPoint X=322.073 Y=105.865 Z=0
    g233: GeomPoint X=318.073 Y=109.865 Z=0
    g234: Circle CenterX=336.157 CenterY=107.779 CenterZ=0 NormalX=0 NormalY=0 NormalZ=1 AngleXU=0 Radius=1
    g235: Circle CenterX=332.651 CenterY=105.853 CenterZ=0 NormalX=0 NormalY=0 NormalZ=1 AngleXU=0 Radius=1
    g236: Circle CenterX=328.643 CenterY=105.865 CenterZ=0 NormalX=0 NormalY=0 NormalZ=1 AngleXU=0 Radius=1
    g237: BSplineCurve PolesCount=3 KnotsCount=2 Degree=2 IsPeriodic=0
    g238: GeomPoint X=336.157 Y=107.779 Z=0
    g239: GeomPoint X=328.643 Y=105.865 Z=0
    g240: LineSegment StartX=322.073 StartY=124.221 StartZ=0 EndX=362.073 EndY=124.221 EndZ=0
    g241: Circle CenterX=371.567 CenterY=-80.8644 CenterZ=0 NormalX=0 NormalY=0 NormalZ=1 AngleXU=0 Radius=1
    g242: Circle CenterX=375.073 CenterY=-82.7896 CenterZ=0 NormalX=0 NormalY=0 NormalZ=1 AngleXU=0 Radius=1
    g243: Circle CenterX=375.073 CenterY=-78.7896 CenterZ=0 NormalX=0 NormalY=0 NormalZ=1 AngleXU=0 Radius=1
    g244: BSplineCurve PolesCount=3 KnotsCount=2 Degree=2 IsPeriodic=0
    g245: GeomPoint X=371.567 Y=-80.8644 Z=0
    g246: GeomPoint X=375.073 Y=-78.7896 Z=0
    g247: Circle CenterX=321.579 CenterY=-53.4075 CenterZ=0 NormalX=0 NormalY=0 NormalZ=1 AngleXU=0 Radius=1
    g248: Circle CenterX=318.073 CenterY=-51.4823 CenterZ=0 NormalX=0 NormalY=0 NormalZ=1 AngleXU=0 Radius=1
    g249: Circle CenterX=318.073 CenterY=-47.4805 CenterZ=0 NormalX=0 NormalY=0 NormalZ=1 AngleXU=0 Radius=1
    g250: BSplineCurve PolesCount=3 KnotsCount=2 Degree=2 IsPeriodic=0
    g251: GeomPoint X=321.579 Y=-53.4075 Z=0
    g252: GeomPoint X=318.073 Y=-47.4805 Z=0
    g253: LineSegment StartX=371.567 StartY=-80.8644 StartZ=0 EndX=321.579 EndY=-53.4075 EndZ=0
    g254: Circle CenterX=321.579 CenterY=-67.3492 CenterZ=0 NormalX=0 NormalY=0 NormalZ=1 AngleXU=0 Radius=1
    g255: Circle CenterX=318.073 CenterY=-65.424 CenterZ=0 NormalX=0 NormalY=0 NormalZ=1 AngleXU=0 Radius=1
    g256: Circle CenterX=318.073 CenterY=-69.424 CenterZ=0 NormalX=0 NormalY=0 NormalZ=1 AngleXU=0 Radius=1
    g257: BSplineCurve PolesCount=3 KnotsCount=2 Degree=2 IsPeriodic=0
    g258: GeomPoint X=321.579 Y=-67.3492 Z=0
    g259: GeomPoint X=318.073 Y=-69.424 Z=0
    g260: Circle CenterX=362.567 CenterY=-89.8542 CenterZ=0 NormalX=0 NormalY=0 NormalZ=1 AngleXU=0 Radius=1
    g261: Circle CenterX=366.073 CenterY=-91.7794 CenterZ=0 NormalX=0 NormalY=0 NormalZ=1 AngleXU=0 Radius=1
    g262: Circle CenterX=362.073 CenterY=-91.7794 CenterZ=0 NormalX=0 NormalY=0 NormalZ=1 AngleXU=0 Radius=1
    g263: BSplineCurve PolesCount=3 KnotsCount=2 Degree=2 IsPeriodic=0
    g264: GeomPoint X=362.567 Y=-89.8542 Z=0
    g265: GeomPoint X=362.073 Y=-91.7794 Z=0
    g266: Circle CenterX=322.073 CenterY=-91.7794 CenterZ=0 NormalX=0 NormalY=0 NormalZ=1 AngleXU=0 Radius=1
    g267: Circle CenterX=318.073 CenterY=-91.7794 CenterZ=0 NormalX=0 NormalY=0 NormalZ=1 AngleXU=0 Radius=1
    g268: Circle CenterX=318.073 CenterY=-87.7794 CenterZ=0 NormalX=0 NormalY=0 NormalZ=1 AngleXU=0 Radius=1
    g269: BSplineCurve PolesCount=3 KnotsCount=2 Degree=2 IsPeriodic=0
    g270: GeomPoint X=322.073 Y=-91.7794 Z=0
    g271: GeomPoint X=318.073 Y=-87.7794 Z=0
    g272: LineSegment StartX=362.567 StartY=-89.8542 StartZ=0 EndX=321.579 EndY=-67.3492 EndZ=0
    g273: LineSegment StartX=318.073 StartY=-69.424 StartZ=0 EndX=318.073 EndY=-87.7794 EndZ=0
    g274: LineSegment StartX=322.073 StartY=-91.7794 StartZ=0 EndX=362.073 EndY=-91.7794 EndZ=0
    g275: Circle CenterX=2.07281 CenterY=124.221 CenterZ=0 NormalX=0 NormalY=0 NormalZ=1 AngleXU=0 Radius=1
    g276: Circle CenterX=1.57905 CenterY=122.295 CenterZ=0 NormalX=0 NormalY=0 NormalZ=1 AngleXU=0 Radius=1
    g277: BSplineCurve PolesCount=3 KnotsCount=2 Degree=2 IsPeriodic=0
    g278: GeomPoint X=2.07281 Y=124.221 Z=0
    g279: GeomPoint X=1.57905 Y=122.295 Z=0
    g280: Circle CenterX=42.0728 CenterY=124.221 CenterZ=0 NormalX=0 NormalY=0 NormalZ=1 AngleXU=0 Radius=1
    g281: Circle CenterX=46.0728 CenterY=124.221 CenterZ=0 NormalX=0 NormalY=0 NormalZ=1 AngleXU=0 Radius=1
    g282: Circle CenterX=46.0728 CenterY=120.221 CenterZ=0 NormalX=0 NormalY=0 NormalZ=1 AngleXU=0 Radius=1
    g283: BSplineCurve PolesCount=3 KnotsCount=2 Degree=2 IsPeriodic=0
    g284: GeomPoint X=42.0728 Y=124.221 Z=0
    g285: GeomPoint X=46.0728 Y=120.221 Z=0
    g286: Circle CenterX=46.0728 CenterY=109.865 CenterZ=0 NormalX=0 NormalY=0 NormalZ=1 AngleXU=0 Radius=1
    g287: Circle CenterX=46.0728 CenterY=105.865 CenterZ=0 NormalX=0 NormalY=0 NormalZ=1 AngleXU=0 Radius=1
    g288: Circle CenterX=42.0728 CenterY=105.865 CenterZ=0 NormalX=0 NormalY=0 NormalZ=1 AngleXU=0 Radius=1
    g289: BSplineCurve PolesCount=3 KnotsCount=2 Degree=2 IsPeriodic=0
    g290: GeomPoint X=46.0728 Y=109.865 Z=0
    g291: GeomPoint X=42.0728 Y=105.865 Z=0
    g292: Circle CenterX=35.5028 CenterY=105.865 CenterZ=0 NormalX=0 NormalY=0 NormalZ=1 AngleXU=0 Radius=1
    g293: Circle CenterX=31.5028 CenterY=105.865 CenterZ=0 NormalX=0 NormalY=0 NormalZ=1 AngleXU=0 Radius=1
    g294: Circle CenterX=27.9965 CenterY=107.79 CenterZ=0 NormalX=0 NormalY=0 NormalZ=1 AngleXU=0 Radius=1
    g295: BSplineCurve PolesCount=3 KnotsCount=2 Degree=2 IsPeriodic=0
    g296: GeomPoint X=35.5028 Y=105.865 Z=0
    g297: GeomPoint X=27.9965 Y=107.79 Z=0
    g298: LineSegment StartX=2.07281 StartY=124.221 StartZ=0 EndX=42.0728 EndY=124.221 EndZ=0
    g299: LineSegment StartX=46.0728 StartY=120.221 StartZ=0 EndX=46.0728 EndY=109.865 EndZ=0
    g300: LineSegment StartX=42.0728 StartY=105.865 StartZ=0 EndX=35.5028 EndY=105.865 EndZ=0
    g301: LineSegment StartX=27.9965 StartY=107.79 StartZ=0 EndX=1.57905 EndY=122.295 EndZ=0
    g302: Circle CenterX=42.5666 CenterY=-67.3492 CenterZ=0 NormalX=0 NormalY=0 NormalZ=1 AngleXU=0 Radius=1
    g303: Circle CenterX=46.0728 CenterY=-65.424 CenterZ=0 NormalX=0 NormalY=0 NormalZ=1 AngleXU=0 Radius=1
    g304: Circle CenterX=46.0728 CenterY=-69.424 CenterZ=0 NormalX=0 NormalY=0 NormalZ=1 AngleXU=0 Radius=1
    g305: BSplineCurve PolesCount=3 KnotsCount=2 Degree=2 IsPeriodic=0
    g306: GeomPoint X=42.5666 Y=-67.3492 Z=0
    g307: GeomPoint X=46.0728 Y=-69.424 Z=0
    g308: Circle CenterX=46.0728 CenterY=-87.7794 CenterZ=0 NormalX=0 NormalY=0 NormalZ=1 AngleXU=0 Radius=1
    g309: Circle CenterX=46.0728 CenterY=-91.7794 CenterZ=0 NormalX=0 NormalY=0 NormalZ=1 AngleXU=0 Radius=1
    g310: Circle CenterX=42.0728 CenterY=-91.7794 CenterZ=0 NormalX=0 NormalY=0 NormalZ=1 AngleXU=0 Radius=1
    g311: BSplineCurve PolesCount=3 KnotsCount=2 Degree=2 IsPeriodic=0
    g312: GeomPoint X=46.0728 Y=-87.7794 Z=0
    g313: GeomPoint X=42.0728 Y=-91.7794 Z=0
    g314: Circle CenterX=2.07281 CenterY=-91.7794 CenterZ=0 NormalX=0 NormalY=0 NormalZ=1 AngleXU=0 Radius=1
    g315: Circle CenterX=-1.92719 CenterY=-91.7794 CenterZ=0 NormalX=0 NormalY=0 NormalZ=1 AngleXU=0 Radius=1
    g316: Circle CenterX=1.57905 CenterY=-89.8542 CenterZ=0 NormalX=0 NormalY=0 NormalZ=1 AngleXU=0 Radius=1
    g317: BSplineCurve PolesCount=3 KnotsCount=2 Degree=2 IsPeriodic=0
    g318: GeomPoint X=2.07281 Y=-91.7794 Z=0
    g319: GeomPoint X=1.57905 Y=-89.8542 Z=0
    g320: LineSegment StartX=2.07281 StartY=-91.7794 StartZ=0 EndX=42.0728 EndY=-91.7794 EndZ=0
    g321: LineSegment StartX=46.0728 StartY=-87.7794 StartZ=0 EndX=46.0728 EndY=-69.424 EndZ=0
    g322: LineSegment StartX=42.5666 StartY=-67.3492 StartZ=0 EndX=1.57905 EndY=-89.8542 EndZ=0
    g323: Circle CenterX=322.073 CenterY=76.4095 CenterZ=0 NormalX=0 NormalY=0 NormalZ=1 AngleXU=0 Radius=4
    g324: BSplineCurve PolesCount=3 KnotsCount=2 Degree=2 IsPeriodic=0
    g325: GeomPoint X=318.073 Y=72.4095 Z=0
    g326: GeomPoint X=322.073 Y=76.4095 Z=0
    g327: Circle CenterX=375.073 CenterY=72.4095 CenterZ=0 NormalX=0 NormalY=0 NormalZ=1 AngleXU=0 Radius=1
    g328: Circle CenterX=375.073 CenterY=76.4095 CenterZ=0 NormalX=0 NormalY=0 NormalZ=1 AngleXU=0 Radius=1
    g329: Circle CenterX=371.073 CenterY=76.4095 CenterZ=0 NormalX=0 NormalY=0 NormalZ=1 AngleXU=0 Radius=1
    g330: BSplineCurve PolesCount=3 KnotsCount=2 Degree=2 IsPeriodic=0
    g331: GeomPoint X=375.073 Y=72.4095 Z=0
    g332: GeomPoint X=371.073 Y=76.4095 Z=0
    g333: LineSegment StartX=322.073 StartY=76.4095 StartZ=0 EndX=371.073 EndY=76.4095 EndZ=0
    g334: LineSegment StartX=318.073 StartY=72.4095 StartZ=0 EndX=318.073 EndY=-47.4805 EndZ=0
    g335: LineSegment StartX=375.073 StartY=72.4095 StartZ=0 EndX=375.073 EndY=-78.7896 EndZ=0
    g336: ArcOfCircle CenterX=-26.9272 CenterY=22.1087 CenterZ=0 NormalX=0 NormalY=0 NormalZ=1 AngleXU=0 Radius=4 StartAngle=5e-16 EndAngle=3.14159
    g337: LineSegment StartX=-22.9272 StartY=22.1087 StartZ=0 EndX=-18.9272 EndY=-83.7794 EndZ=0
    g338: LineSegment StartX=-34.9272 StartY=-83.7794 StartZ=0 EndX=-30.9272 EndY=22.1087 EndZ=0
    g339: ArcOfCircle CenterX=391.073 CenterY=22.1087 CenterZ=0 NormalX=0 NormalY=0 NormalZ=1 AngleXU=0 Radius=4 StartAngle=0 EndAngle=3.14159
    g340: LineSegment StartX=387.073 StartY=22.1087 StartZ=0 EndX=383.073 EndY=-83.7794 EndZ=0
    g341: LineSegment StartX=395.073 StartY=22.1087 StartZ=0 EndX=399.073 EndY=-83.7794 EndZ=0
    g342: Circle CenterX=-10.9272 CenterY=-78.7794 CenterZ=0 NormalX=0 NormalY=0 NormalZ=1 AngleXU=0 Radius=1
    g343: Circle CenterX=-10.9272 CenterY=-82.7794 CenterZ=0 NormalX=0 NormalY=0 NormalZ=1 AngleXU=0 Radius=1
    g344: Circle CenterX=-7.42095 CenterY=-80.8542 CenterZ=0 NormalX=0 NormalY=0 NormalZ=1 AngleXU=0 Radius=1
    g345: BSplineCurve PolesCount=3 KnotsCount=2 Degree=2 IsPeriodic=0
    g346: GeomPoint X=-10.9272 Y=-78.7794 Z=0
    g347: GeomPoint X=-7.42095 Y=-80.8542 Z=0
    g348: Circle CenterX=42.5666 CenterY=-53.4075 CenterZ=0 NormalX=0 NormalY=0 NormalZ=1 AngleXU=0 Radius=1
    g349: Circle CenterX=46.0728 CenterY=-51.4823 CenterZ=0 NormalX=0 NormalY=0 NormalZ=1 AngleXU=0 Radius=1
    g350: Circle CenterX=46.0728 CenterY=-47.4823 CenterZ=0 NormalX=0 NormalY=0 NormalZ=1 AngleXU=0 Radius=1
    g351: BSplineCurve PolesCount=3 KnotsCount=2 Degree=2 IsPeriodic=0
    g352: GeomPoint X=42.5666 Y=-53.4075 Z=0
    g353: GeomPoint X=46.0728 Y=-47.4823 Z=0
    g354: Circle CenterX=46.0728 CenterY=72.4095 CenterZ=0 NormalX=0 NormalY=0 NormalZ=1 AngleXU=0 Radius=1
    g355: Circle CenterX=46.0728 CenterY=76.4095 CenterZ=0 NormalX=0 NormalY=0 NormalZ=1 AngleXU=0 Radius=1
    g356: Circle CenterX=42.0728 CenterY=76.4095 CenterZ=0 NormalX=0 NormalY=0 NormalZ=1 AngleXU=0 Radius=1
    g357: BSplineCurve PolesCount=3 KnotsCount=2 Degree=2 IsPeriodic=0
    g358: GeomPoint X=46.0728 Y=72.4095 Z=0
    g359: GeomPoint X=42.0728 Y=76.4095 Z=0
    g360: Circle CenterX=-6.92718 CenterY=76.4095 CenterZ=0 NormalX=0 NormalY=0 NormalZ=1 AngleXU=0 Radius=1
    g361: Circle CenterX=-10.9272 CenterY=76.4095 CenterZ=0 NormalX=0 NormalY=0 NormalZ=1 AngleXU=0 Radius=1
    g362: Circle CenterX=-10.9272 CenterY=72.4095 CenterZ=0 NormalX=0 NormalY=0 NormalZ=1 AngleXU=0 Radius=1
    g363: BSplineCurve PolesCount=3 KnotsCount=2 Degree=2 IsPeriodic=0
    g364: GeomPoint X=-6.92718 Y=76.4095 Z=0
    g365: GeomPoint X=-10.9272 Y=72.4095 Z=0
    g366: LineSegment StartX=-10.9272 StartY=72.4095 StartZ=0 EndX=-10.9272 EndY=-78.7794 EndZ=0
    g367: LineSegment StartX=-7.42095 StartY=-80.8542 StartZ=0 EndX=42.5666 EndY=-53.4075 EndZ=0
    g368: LineSegment StartX=46.0728 StartY=-47.4823 StartZ=0 EndX=46.0728 EndY=72.4095 EndZ=0
    g369: LineSegment StartX=42.0728 StartY=76.4095 StartZ=0 EndX=-6.92719 EndY=76.4095 EndZ=0
    g370: LineSegment StartX=232.072 StartY=136.221 StartZ=0 EndX=232.072 EndY=-117.815 EndZ=0
    g371: LineSegment StartX=132.072 StartY=136.221 StartZ=0 EndX=132.072 EndY=-121.309 EndZ=0
    g372: LineSegment StartX=245.072 StartY=136.221 StartZ=0 EndX=245.072 EndY=-116.499 EndZ=0
    g373: LineSegment StartX=119.072 StartY=136.221 StartZ=0 EndX=119.072 EndY=-116.228 EndZ=0
    g374: LineSegment StartX=-42.9272 StartY=136.221 StartZ=0 EndX=407.073 EndY=136.221 EndZ=0
    g375: LineSegment StartX=232.072 StartY=136.221 StartZ=0 EndX=220.072 EndY=136.221 EndZ=0
    g376: LineSegment StartX=232.072 StartY=136.221 StartZ=0 EndX=232.072 EndY=124.221 EndZ=0
    g377: LineSegment StartX=220.072 StartY=136.221 StartZ=0 EndX=220.072 EndY=124.221 EndZ=0
    g378: LineSegment StartX=220.072 StartY=136.221 StartZ=0 EndX=226.072 EndY=136.221 EndZ=0
    g379: LineSegment StartX=220.072 StartY=136.221 StartZ=0 EndX=220.072 EndY=130.221 EndZ=0
    g380: LineSegment StartX=220.072 StartY=124.221 StartZ=0 EndX=226.072 EndY=124.221 EndZ=0
    g381: LineSegment StartX=232.072 StartY=124.221 StartZ=0 EndX=232.072 EndY=127.221 EndZ=0
    g382: LineSegment StartX=232.072 StartY=136.221 StartZ=0 EndX=232.072 EndY=133.221 EndZ=0
    g383-g387: Circle x5 (B-spline internal-alignment scaffolding for g388; pole/knot coordinates omitted)
    g388: BSplineCurve PolesCount=5 KnotsCount=3 Degree=3 IsPeriodic=0
    g389: GeomPoint X=232.072 Y=133.221 Z=0
    g390: GeomPoint X=223.072 Y=130.221 Z=0
    g391: GeomPoint X=232.072 Y=127.221 Z=0
    g392: LineSegment StartX=189.124 StartY=124.221 StartZ=0 EndX=302.073 EndY=124.221 EndZ=0
    g393: LineSegment StartX=132.072 StartY=136.221 StartZ=0 EndX=132.072 EndY=124.221 EndZ=0
    g394: LineSegment StartX=132.072 StartY=136.221 StartZ=0 EndX=144.072 EndY=136.221 EndZ=0
    g395: LineSegment StartX=144.072 StartY=136.221 StartZ=0 EndX=144.072 EndY=124.221 EndZ=0
    g396: LineSegment StartX=144.072 StartY=124.221 StartZ=0 EndX=138.072 EndY=124.221 EndZ=0
    g397: LineSegment StartX=144.072 StartY=136.221 StartZ=0 EndX=138.072 EndY=136.221 EndZ=0
    g398: LineSegment StartX=144.072 StartY=136.221 StartZ=0 EndX=144.072 EndY=130.221 EndZ=0
    g399: LineSegment StartX=133.152 StartY=132.86 StartZ=0 EndX=133.152 EndY=129.86 EndZ=0
  constraints (678):
    c: Vertical(g0)
    c: Vertical(g1)
    c: Block(g1)
    c: Block(g0)
    c: Weight(g4) = 1
    c: Equal(g4,g5)
    c: Equal(g4,g6)
    c: InternalAlignment(g4,g7)
    c: InternalAlignment(g5,g7)
    c: InternalAlignment(g6,g7)
    c: InternalAlignment(g8,g7)
    c: InternalAlignment(g9,g7)
    c: Weight(g10) = 1
    c: Equal(g10,g11)
    c: Equal(g10,g12)
    c: InternalAlignment(g10,g13)
    c: InternalAlignment(g11,g13)
    c: InternalAlignment(g12,g13)
    c: InternalAlignment(g14,g13)
    c: InternalAlignment(g15,g13)
    c: Block(g13)
    c: Block(g7)
    c: Weight(g16) = 1
    c: Equal(g16,g17)
    c: Equal(g16,g18)
    c: InternalAlignment(g16,g19)
    c: InternalAlignment(g17,g19)
    c: InternalAlignment(g18,g19)
    c: InternalAlignment(g20,g19)
    c: InternalAlignment(g21,g19)
    c: Weight(g22) = 1
    c: Equal(g22,g23)
    c: Equal(g22,g24)
    c: InternalAlignment(g22,g25)
    c: InternalAlignment(g23,g25)
    c: InternalAlignment(g24,g25)
    c: InternalAlignment(g26,g25)
    c: InternalAlignment(g27,g25)
    c: Block(g25)
    c: Block(g19)
    c: Weight(g28) = 1
    c: Equal(g28,g29)
    c: Equal(g28,g30)
    c: InternalAlignment(g28,g31)
    c: InternalAlignment(g29,g31)
    c: InternalAlignment(g30,g31)
    c: InternalAlignment(g32,g31)
    c: InternalAlignment(g33,g31)
    c: Weight(g34) = 1
    c: Equal(g34,g35)
    c: Equal(g34,g36)
    c: InternalAlignment(g34,g37)
    c: InternalAlignment(g35,g37)
    c: InternalAlignment(g36,g37)
    c: InternalAlignment(g38,g37)
    c: InternalAlignment(g39,g37)
    c: Block(g31)
    c: Block(g37)
    c: Coincident(g40,g1)
    c: Coincident(g40,g0)
    c: Horizontal(g40)
    c: Distance(g40) = 450
    c: Weight(g41) = 1
    c: Equal(g41,g42)
    c: Equal(g41,g43)
    c: InternalAlignment(g41,g44)
    c: InternalAlignment(g42,g44)
    c: InternalAlignment(g43,g44)
    c: InternalAlignment(g45,g44)
    c: InternalAlignment(g46,g44)
    c: Block(g44)
    c: Weight(g47) = 1
    c: Equal(g47,g48)
    c: Equal(g47,g49)
    c: InternalAlignment(g47,g50)
    c: InternalAlignment(g48,g50)
    c: InternalAlignment(g49,g50)
    c: InternalAlignment(g51,g50)
    c: InternalAlignment(g52,g50)
    c: Block(g50)
    c: Weight(g53) = 1
    c: Equal(g53,g54)
    c: Equal(g53,g55)
    c: InternalAlignment(g53,g56)
    c: InternalAlignment(g54,g56)
    c: InternalAlignment(g55,g56)
    c: InternalAlignment(g57,g56)
    c: InternalAlignment(g58,g56)
    c: Block(g56)
    c: Weight(g59) = 1
    c: Equal(g59,g60)
    c: Equal(g59,g61)
    c: InternalAlignment(g59,g62)
    c: InternalAlignment(g60,g62)
    c: InternalAlignment(g61,g62)
    c: InternalAlignment(g63,g62)
    c: InternalAlignment(g64,g62)
    c: Block(g62)
    c: Weight(g65) = 1
    c: Equal(g65,g66)
    c: Equal(g65,g67)
    c: InternalAlignment(g65,g68)
    c: InternalAlignment(g66,g68)
    c: InternalAlignment(g67,g68)
    c: InternalAlignment(g69,g68)
    c: InternalAlignment(g70,g68)
    c: Weight(g71) = 1
    c: Equal(g71,g72)
    c: Equal(g71,g73)
    c: InternalAlignment(g71,g74)
    c: InternalAlignment(g72,g74)
    c: InternalAlignment(g73,g74)
    c: InternalAlignment(g75,g74)
    c: InternalAlignment(g76,g74)
    c: Block(g68)
    c: Block(g74)
    c: Coincident(g77,g68)
    c: Coincident(g77,g74)
    c: Vertical(g77)
    c: Coincident(g78,g68)
    c: Coincident(g78,g50)
    c: Coincident(g79,g50)
    c: Coincident(g79,g74)
    c: Weight(g80) = 1
    c: Equal(g80,g81)
    c: Equal(g80,g82)
    c: InternalAlignment(g80,g83)
    c: InternalAlignment(g81,g83)
    c: InternalAlignment(g82,g83)
    c: InternalAlignment(g84,g83)
    c: InternalAlignment(g85,g83)
    c: Weight(g86) = 1
    c: Equal(g86,g87)
    c: Equal(g86,g88)
    c: InternalAlignment(g86,g89)
    c: InternalAlignment(g87,g89)
    c: InternalAlignment(g88,g89)
    c: InternalAlignment(g90,g89)
    c: InternalAlignment(g91,g89)
    c: Block(g83)
    c: Block(g89)
    c: Coincident(g92,g83)
    c: Coincident(g92,g89)
    c: Vertical(g92)
    c: Coincident(g93,g83)
    c: Coincident(g93,g44)
    c: Coincident(g94,g44)
    c: Coincident(g94,g89)
    c: Weight(g95) = 1
    c: Equal(g95,g96)
    c: Equal(g95,g97)
    c: InternalAlignment(g95,g98)
    c: InternalAlignment(g96,g98)
    c: InternalAlignment(g97,g98)
    c: InternalAlignment(g99,g98)
    c: InternalAlignment(g100,g98)
    c: Weight(g101) = 1
    c: Equal(g101,g102)
    c: Equal(g101,g103)
    c: InternalAlignment(g101,g104)
    c: InternalAlignment(g102,g104)
    c: InternalAlignment(g103,g104)
    c: InternalAlignment(g105,g104)
    c: InternalAlignment(g106,g104)
    c: Block(g98)
    c: Block(g104)
    c: Coincident(g107,g98)
    c: Coincident(g107,g104)
    c: Vertical(g107)
    c: Coincident(g108,g104)
    c: Coincident(g108,g62)
    c: Coincident(g109,g62)
    c: Coincident(g109,g98)
    c: Weight(g110) = 1
    c: Equal(g110,g111)
    c: Equal(g110,g112)
    c: InternalAlignment(g110,g113)
    c: InternalAlignment(g111,g113)
    c: InternalAlignment(g112,g113)
    c: InternalAlignment(g114,g113)
    c: InternalAlignment(g115,g113)
    c: Weight(g116) = 1
    c: Equal(g116,g117)
    c: Equal(g116,g118)
    c: InternalAlignment(g116,g119)
    c: InternalAlignment(g117,g119)
    c: InternalAlignment(g118,g119)
    c: InternalAlignment(g120,g119)
    c: InternalAlignment(g121,g119)
    c: Block(g113)
    c: Block(g119)
    c: Coincident(g122,g113)
    c: Coincident(g122,g119)
    c: Vertical(g122)
    c: Coincident(g123,g119)
    c: Coincident(g123,g56)
    c: Coincident(g124,g56)
    c: Coincident(g124,g113)
    c: Weight(g125) = 1
    c: Equal(g125,g126)
    c: Equal(g125,g127)
    c: InternalAlignment(g125,g128)
    c: InternalAlignment(g126,g128)
    c: InternalAlignment(g127,g128)
    c: InternalAlignment(g129,g128)
    c: InternalAlignment(g130,g128)
    c: Weight(g131) = 1
    c: Equal(g131,g132)
    c: Equal(g131,g133)
    c: InternalAlignment(g131,g134)
    c: InternalAlignment(g132,g134)
    c: InternalAlignment(g133,g134)
    c: InternalAlignment(g135,g134)
    c: InternalAlignment(g136,g134)
    c: Weight(g137) = 1
    c: Equal(g137,g138)
    c: Equal(g137,g139)
    c: InternalAlignment(g137,g140)
    c: InternalAlignment(g138,g140)
    c: InternalAlignment(g139,g140)
    c: InternalAlignment(g141,g140)
    c: InternalAlignment(g142,g140)
    c: Weight(g143) = 1
    c: Equal(g143,g144)
    c: Equal(g143,g145)
    c: InternalAlignment(g143,g146)
    c: InternalAlignment(g144,g146)
    c: InternalAlignment(g145,g146)
    c: InternalAlignment(g147,g146)
    c: InternalAlignment(g148,g146)
    c: Block(g146)
    c: Block(g140)
    c: Block(g134)
    c: Block(g128)
    c: Coincident(g149,g25)
    c: Coincident(g149,g146)
    c: Coincident(g150,g146)
    c: Coincident(g150,g140)
    c: Horizontal(g150)
    c: Coincident(g151,g140)
    c: Coincident(g151,g25)
    c: Vertical(g151)
    c: Coincident(g152,g19)
    c: Coincident(g152,g134)
    c: Vertical(g152)
    c: Coincident(g153,g134)
    c: Coincident(g153,g128)
    c: Horizontal(g153)
    c: Coincident(g154,g128)
    c: Coincident(g154,g19)
    c: Weight(g155) = 1
    c: Equal(g155,g156)
    c: Equal(g155,g157)
    c: InternalAlignment(g155,g158)
    c: InternalAlignment(g156,g158)
    c: InternalAlignment(g157,g158)
    c: InternalAlignment(g159,g158)
    c: InternalAlignment(g160,g158)
    c: Weight(g161) = 1
    c: Equal(g161,g162)
    c: Equal(g161,g163)
    c: InternalAlignment(g161,g164)
    c: InternalAlignment(g162,g164)
    c: InternalAlignment(g163,g164)
    c: InternalAlignment(g165,g164)
    c: InternalAlignment(g166,g164)
    c: Weight(g167) = 1
    c: Equal(g167,g168)
    c: Equal(g167,g169)
    c: InternalAlignment(g167,g170)
    c: InternalAlignment(g168,g170)
    c: InternalAlignment(g169,g170)
    c: InternalAlignment(g171,g170)
    c: InternalAlignment(g172,g170)
    c: Weight(g173) = 1
    c: Equal(g173,g174)
    c: Equal(g173,g175)
    c: InternalAlignment(g173,g176)
    c: InternalAlignment(g174,g176)
    c: InternalAlignment(g175,g176)
    c: InternalAlignment(g177,g176)
    c: InternalAlignment(g178,g176)
    c: Block(g176)
    c: Block(g170)
    c: Block(g164)
    c: Block(g158)
    c: Coincident(g179,g170)
    c: Coincident(g179,g7)
    c: Vertical(g179)
    c: Coincident(g180,g13)
    c: Coincident(g180,g164)
    c: Vertical(g180)
    c: Coincident(g181,g158)
    c: Coincident(g181,g13)
    c: Coincident(g182,g7)
    c: Weight(g183) = 1
    c: Equal(g183,g184)
    c: Equal(g183,g185)
    c: InternalAlignment(g183,g186)
    c: InternalAlignment(g184,g186)
    c: InternalAlignment(g185,g186)
    c: InternalAlignment(g187,g186)
    c: InternalAlignment(g188,g186)
    c: Weight(g189) = 1
    c: Equal(g189,g190)
    c: Equal(g189,g191)
    c: InternalAlignment(g189,g192)
    c: InternalAlignment(g190,g192)
    c: InternalAlignment(g191,g192)
    c: InternalAlignment(g193,g192)
    c: InternalAlignment(g194,g192)
    c: Block(g192)
    c: Block(g186)
    c: Coincident(g195,g192)
    c: Coincident(g195,g31)
    c: Coincident(g196,g31)
    c: Coincident(g196,g186)
    c: Coincident(g197,g186)
    c: Coincident(g197,g192)
    c: Vertical(g197)
    c: Weight(g198) = 1
    c: Equal(g198,g199)
    c: Equal(g198,g200)
    c: InternalAlignment(g198,g201)
    c: InternalAlignment(g199,g201)
    c: InternalAlignment(g200,g201)
    c: InternalAlignment(g202,g201)
    c: InternalAlignment(g203,g201)
    c: Weight(g204) = 1
    c: Equal(g204,g205)
    c: Equal(g204,g206)
    c: InternalAlignment(g204,g207)
    c: InternalAlignment(g205,g207)
    c: InternalAlignment(g206,g207)
    c: InternalAlignment(g208,g207)
    c: InternalAlignment(g209,g207)
    c: Block(g207)
    c: Block(g201)
    c: Coincident(g210,g201)
    c: Coincident(g210,g37)
    c: Coincident(g211,g37)
    c: Coincident(g211,g207)
    c: Coincident(g212,g207)
    c: Coincident(g212,g201)
    c: Vertical(g212)
    c: Horizontal(g213)
    c: Block(g213)
    c: Vertical(g214)
    c: Block(g214)
    c: Block(g215)
    c: Weight(g216) = 1
    c: Equal(g216,g217)
    c: Equal(g216,g218)
    c: InternalAlignment(g216,g219)
    c: InternalAlignment(g217,g219)
    c: InternalAlignment(g218,g219)
    c: InternalAlignment(g220,g219)
    c: InternalAlignment(g221,g219)
    c: Weight(g222) = 1
    c: Equal(g222,g223)
    c: Equal(g222,g224)
    c: InternalAlignment(g222,g225)
    c: InternalAlignment(g223,g225)
    c: InternalAlignment(g224,g225)
    c: InternalAlignment(g226,g225)
    c: InternalAlignment(g227,g225)
    c: Weight(g228) = 1
    c: Equal(g228,g229)
    c: Equal(g228,g230)
    c: InternalAlignment(g228,g231)
    c: InternalAlignment(g229,g231)
    c: InternalAlignment(g230,g231)
    c: InternalAlignment(g232,g231)
    c: InternalAlignment(g233,g231)
    c: Weight(g234) = 1
    c: Equal(g234,g235)
    c: Equal(g234,g236)
    c: InternalAlignment(g234,g237)
    c: InternalAlignment(g235,g237)
    c: InternalAlignment(g236,g237)
    c: InternalAlignment(g238,g237)
    c: InternalAlignment(g239,g237)
    c: Block(g219)
    c: Block(g225)
    c: Block(g231)
    c: Block(g237)
    c: Coincident(g240,g225)
    c: Coincident(g240,g219)
    c: Horizontal(g240)
    c: Block(g182)
    c: Weight(g241) = 1
    c: Equal(g241,g242)
    c: Equal(g241,g243)
    c: InternalAlignment(g241,g244)
    c: InternalAlignment(g242,g244)
    c: InternalAlignment(g243,g244)
    c: InternalAlignment(g245,g244)
    c: InternalAlignment(g246,g244)
    c: Weight(g247) = 1
    c: Equal(g247,g248)
    c: Equal(g247,g249)
    c: InternalAlignment(g247,g250)
    c: InternalAlignment(g248,g250)
    c: InternalAlignment(g249,g250)
    c: InternalAlignment(g251,g250)
    c: InternalAlignment(g252,g250)
    c: Block(g244)
    c: Block(g250)
    c: Coincident(g253,g244)
    c: Coincident(g253,g250)
    c: Weight(g254) = 1
    c: Equal(g254,g255)
    c: Equal(g254,g256)
    c: InternalAlignment(g254,g257)
    c: InternalAlignment(g255,g257)
    c: InternalAlignment(g256,g257)
    c: InternalAlignment(g258,g257)
    c: InternalAlignment(g259,g257)
    c: Weight(g260) = 1
    c: Equal(g260,g261)
    c: Equal(g260,g262)
    c: InternalAlignment(g260,g263)
    c: InternalAlignment(g261,g263)
    c: InternalAlignment(g262,g263)
    c: InternalAlignment(g264,g263)
    c: InternalAlignment(g265,g263)
    c: Weight(g266) = 1
    c: Equal(g266,g267)
    c: Equal(g266,g268)
    c: InternalAlignment(g266,g269)
    c: InternalAlignment(g267,g269)
    c: InternalAlignment(g268,g269)
    c: InternalAlignment(g270,g269)
    c: InternalAlignment(g271,g269)
    c: Block(g269)
    c: Block(g263)
    c: Block(g257)
    c: Coincident(g272,g263)
    c: Coincident(g272,g257)
    c: Coincident(g273,g257)
    c: Coincident(g273,g269)
    c: Vertical(g273)
    c: Coincident(g274,g269)
    c: Coincident(g274,g263)
    c: Horizontal(g274)
    c: Weight(g275) = 1
    c: Equal(g275,g276)
    c: InternalAlignment(g275,g277)
    c: InternalAlignment(g276,g277)
    c: InternalAlignment(g278,g277)
    c: InternalAlignment(g279,g277)
    c: Weight(g280) = 1
    c: InternalAlignment(g281,g283)
    c: InternalAlignment(g282,g283)
    c: InternalAlignment(g284,g283)
    c: InternalAlignment(g285,g283)
    c: Weight(g286) = 1
    c: Equal(g286,g287)
    c: Equal(g286,g288)
    c: InternalAlignment(g286,g289)
    c: InternalAlignment(g287,g289)
    c: InternalAlignment(g288,g289)
    c: InternalAlignment(g290,g289)
    c: InternalAlignment(g291,g289)
    c: Equal(g292,g293)
    c: Equal(g292,g294)
    c: InternalAlignment(g292,g295)
    c: InternalAlignment(g293,g295)
    c: InternalAlignment(g294,g295)
    c: InternalAlignment(g296,g295)
    c: InternalAlignment(g297,g295)
    c: Block(g283)
    c: Block(g289)
    c: Block(g295)
    c: Block(g277)
    c: Coincident(g298,g277)
    c: Coincident(g298,g283)
    c: Horizontal(g298)
    c: Coincident(g299,g283)
    c: Coincident(g299,g289)
    c: Vertical(g299)
    c: Coincident(g300,g289)
    c: Coincident(g300,g295)
    c: Horizontal(g300)
    c: Coincident(g301,g295)
    c: Coincident(g301,g277)
    c: Weight(g302) = 1
    c: Equal(g302,g303)
    c: Equal(g302,g304)
    c: InternalAlignment(g302,g305)
    c: InternalAlignment(g303,g305)
    c: InternalAlignment(g304,g305)
    c: InternalAlignment(g306,g305)
    c: InternalAlignment(g307,g305)
    c: Weight(g308) = 1
    c: Equal(g308,g309)
    c: Equal(g308,g310)
    c: InternalAlignment(g308,g311)
    c: InternalAlignment(g309,g311)
    c: InternalAlignment(g310,g311)
    c: InternalAlignment(g312,g311)
    c: Weight(g314) = 1
    c: Equal(g314,g315)
    c: Equal(g314,g316)
    c: InternalAlignment(g314,g317)
    c: InternalAlignment(g315,g317)
    c: InternalAlignment(g316,g317)
    c: InternalAlignment(g318,g317)
    c: InternalAlignment(g319,g317)
    c: Block(g317)
    c: Block(g311)
    c: Block(g305)
    c: Coincident(g320,g317)
    c: Coincident(g320,g311)
    c: Horizontal(g320)
    c: Coincident(g321,g311)
    c: Coincident(g321,g305)
    c: Vertical(g321)
    c: Coincident(g322,g305)
    c: Coincident(g322,g317)
    c: InternalAlignment(g323,g324)
    c: InternalAlignment(g325,g324)
    c: InternalAlignment(g326,g324)
    c: Block(g324)
    c: Equal(g327,g328)
    c: Equal(g327,g329)
    c: InternalAlignment(g327,g330)
    c: InternalAlignment(g328,g330)
    c: InternalAlignment(g329,g330)
    c: InternalAlignment(g331,g330)
    c: InternalAlignment(g332,g330)
    c: Block(g330)
    c: Coincident(g333,g324)
    c: Horizontal(g333)
    c: Block(g333)
    c: Coincident(g334,g324)
    c: Coincident(g334,g250)
    c: Vertical(g334)
    c: Coincident(g335,g330)
    c: Coincident(g335,g244)
    c: Vertical(g335)
    c: Block(g336)
    c: Block(g2)
    c: Distance(g334) = 119.89
    c: Coincident(g337,g336)
    c: Coincident(g337,g2)
    c: Coincident(g338,g2)
    c: Coincident(g338,g336)
    c: Block(g3)
    c: Block(g339)
    c: Coincident(g340,g339)
    c: Coincident(g340,g3)
    c: Coincident(g341,g339)
    c: Coincident(g341,g3)
    c: Block(g341)
    c: Block(g340)
    c: Weight(g342) = 1
    c: Equal(g342,g343)
    c: Equal(g342,g344)
    c: InternalAlignment(g342,g345)
    c: InternalAlignment(g343,g345)
    c: InternalAlignment(g344,g345)
    c: InternalAlignment(g346,g345)
    c: InternalAlignment(g347,g345)
    c: Weight(g348) = 1
    c: Equal(g348,g349)
    c: Equal(g348,g350)
    c: InternalAlignment(g348,g351)
    c: InternalAlignment(g349,g351)
    c: InternalAlignment(g350,g351)
    c: InternalAlignment(g352,g351)
    c: InternalAlignment(g353,g351)
    c: Weight(g354) = 1
    c: Equal(g354,g355)
    c: Equal(g354,g356)
    c: InternalAlignment(g354,g357)
    c: InternalAlignment(g355,g357)
    c: InternalAlignment(g356,g357)
    c: InternalAlignment(g358,g357)
    c: InternalAlignment(g359,g357)
    c: Weight(g360) = 1
    c: Equal(g360,g361)
    c: Equal(g360,g362)
    c: InternalAlignment(g360,g363)
    c: InternalAlignment(g361,g363)
    c: InternalAlignment(g362,g363)
    c: InternalAlignment(g364,g363)
    c: InternalAlignment(g365,g363)
    c: Block(g363)
    c: Block(g357)
    c: Block(g351)
    c: Block(g345)
    c: Coincident(g366,g363)
    c: Coincident(g366,g345)
    c: Vertical(g366)
    c: Coincident(g367,g345)
    c: Coincident(g367,g351)
    c: Coincident(g368,g351)
    c: Coincident(g368,g357)
    c: Vertical(g368)
    c: Coincident(g369,g357)
    c: Coincident(g369,g363)
    c: Horizontal(g369)
    c: Vertical(g370)
    c: Vertical(g371)
    c: Vertical(g372)
    c: Vertical(g373)
    c: Coincident(g374,g0)
    c: Coincident(g374,g1)
    c: Horizontal(g374)
    c: Block(g374)
    c: Distance(g374) = 450
    c: Block(g372)
    c: Block(g370)
    c: Block(g371)
    c: Block(g373)
    c: Distance(g0) = 240
    c: Horizontal(g375)
    c: Distance(g375) = 12
    c: Coincident(g375,g370)
    c: Vertical(g376)
    c: Distance(g376) = 12
    c: Coincident(g376,g370)
    c: Coincident(g377,g375)
    c: Vertical(g377)
    c: Horizontal(g378)
    c: Vertical(g379)
    c: Distance(g379) = 6
    c: Coincident(g379,g375)
    c: Coincident(g378,g375)
    c: Block(g377)
    c: Coincident(g380,g377)
    c: Horizontal(g380)
    c: Distance(g380) = 6
    c: Vertical(g381)
    c: Distance(g381) = 3
    c: Vertical(g382)
    c: Distance(g382) = 3
    c: Coincident(g382,g370)
    c: Coincident(g376,g381)
    c: Coincident(g388,g382)
    c: Weight(g383) = 1
    c: Equal(g383,g384)
    c: Coincident(g384,g378)
    c: Equal(g383,g385)
    c: Coincident(g385,g379)
    c: Equal(g383,g386)
    c: Coincident(g386,g380)
    c: Equal(g383,g387)
    c: Coincident(g388,g381)
    c: InternalAlignment(g383-g387 -> g388) x5
    c: InternalAlignment(g389,g388)
    c: InternalAlignment(g390,g388)
    c: InternalAlignment(g391,g388)
    c: Coincident(g392,g164)
    c: Coincident(g392,g158)
    c: Horizontal(g392)
    c: Block(g388)
    c: Vertical(g393)
    c: Distance(g393) = 12
    c: Coincident(g393,g371)
    c: Horizontal(g394)
    c: Distance(g394) = 12
    c: Coincident(g394,g371)
    c: Coincident(g395,g394)
    c: Vertical(g395)
    c: Distance(g395) = 12
    c: Coincident(g396,g395)
    c: Horizontal(g396)
    c: Distance(g396) = 6
    c: Horizontal(g397)
    c: Distance(g397) = 6
    c: Coincident(g397,g394)
    c: Vertical(g398)
    c: Distance(g398) = 6
    c: Coincident(g398,g394)
    c: Vertical(g399)
    c: Distance(g399) = 3
FEATURE [Part::Extrusion] Extrude005
  Base = -> Sketch003
  Dir = (0,0,1)
  DirMode = 2
  FaceMakerClass = Part::FaceMakerBullseye
  LengthFwd = 24
  LengthRev = 0
  Solid = true
  Symmetric = false
